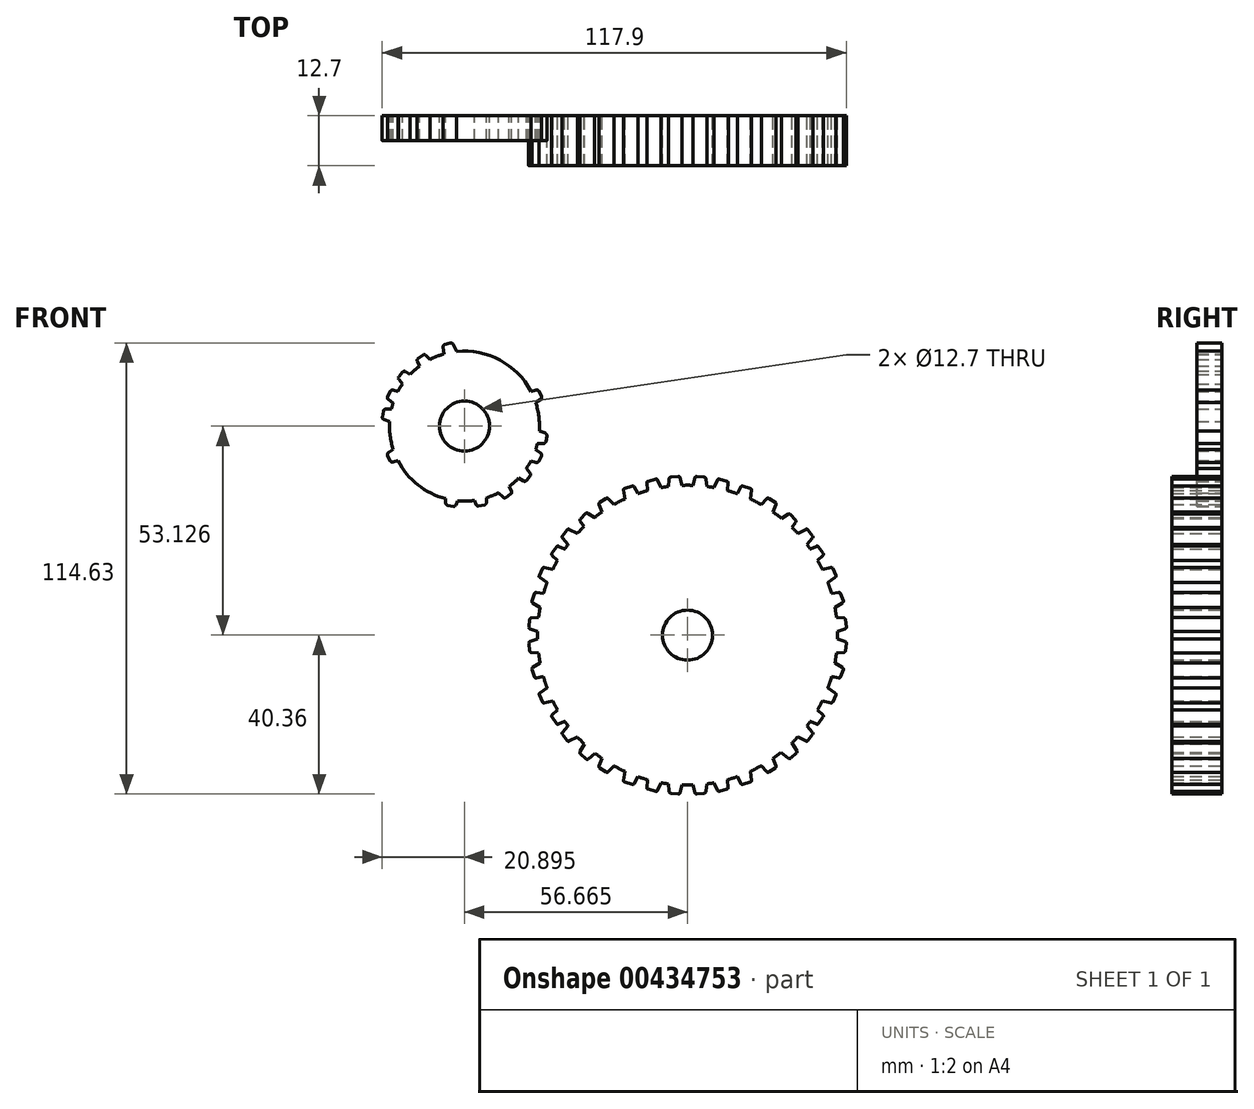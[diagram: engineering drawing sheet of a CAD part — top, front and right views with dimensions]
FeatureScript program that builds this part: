
annotation { "Feature Type Name" : "Feature", "Feature Type Description" : "" }
export const myFeature = defineFeature(function(context is Context, id is Id, definition is map)
    precondition{}
    {
        {
            var Q0;
            Q0=qCreatedBy(makeId("Front.planeOp"),FACE);
            var sketch = newSketch(context, id + "F0", { "sketchPlane" : qUnion([Q0])});
            skCircle(sketch, "E0", {"center": v(0, 0) * mm, "radius": 38.1 * mm});
            skCircle(sketch, "E1", {"center": v(0, 0) * mm, "radius": 6.35 * mm});
            skSolve(sketch);
        }
        {
            var Q0;
            Q0=makeQuery(id+"F0.imprint","IMPRINT",FACE,{"disambiguationData":[TD([[makeQuery(id+"F0.imprint","IMPRINT",EDGE,{"derivedFrom":sQuery(id+"F0.wireOp",EDGE,"E0")}),1.0]])]});
            extrude(context, id + "F1", {"entities" : qUnion([Q0]), "depth" : 12.7 * mm});
        }
        {
            var Q0;
            Q0=qCreatedBy(makeId("Front.planeOp"),FACE);
            var sketch = newSketch(context, id + "F2", { "sketchPlane" : qUnion([Q0])});
            skCircle(sketch, "E2", {"center": v(-56.67, 53.13) * mm, "radius": 19.05 * mm});
            skCircle(sketch, "E3", {"center": v(-56.67, 53.13) * mm, "radius": 6.35 * mm});
            skSolve(sketch);
        }
        {
            var Q0;
            Q0 = qSketchRegion(id + "F2", true);
            extrude(context, id + "F3", {"entities" : qUnion([Q0]), "depth" : 6.35 * mm});
        }
        {
            var Q0;
            Q0=qCreatedBy(makeId("Front.planeOp"),FACE);
            var sketch = newSketch(context, id + "F4", { "sketchPlane" : qUnion([Q0])});
            skLineSegment(sketch, "E4", {"start": v(-9.65, 35.42) * mm, "end": v(-6.58, 36.24) * mm});
            skLineSegment(sketch, "E5", {"start": v(-10.34, 38.75) * mm, "end": v(-10.2, 37.16) * mm});
            skLineSegment(sketch, "E6", {"start": v(-10.09, 39.1) * mm, "end": v(-8.05, 39.65) * mm});
            skLineSegment(sketch, "E7", {"start": v(-7.65, 39.47) * mm, "end": v(-6.37, 36.7) * mm});
            skLineSegment(sketch, "E8", {"start": v(-15.4, 33.61) * mm, "end": v(-12.37, 34.6) * mm});
            skLineSegment(sketch, "E9", {"start": v(-16.25, 36.9) * mm, "end": v(-15.83, 33.88) * mm});
            skLineSegment(sketch, "E10", {"start": v(-16.02, 37.27) * mm, "end": v(-14.01, 37.92) * mm});
            skLineSegment(sketch, "E11", {"start": v(-13.6, 37.76) * mm, "end": v(-12.18, 35.07) * mm});
            skLineSegment(sketch, "E12", {"start": v(-20.77, 30.34) * mm, "end": v(-18.25, 31.93) * mm});
            skLineSegment(sketch, "E13", {"start": v(-22.47, 33.21) * mm, "end": v(-21.38, 30.54) * mm});
            skLineSegment(sketch, "E14", {"start": v(-22.3, 33.72) * mm, "end": v(-20.7, 34.74) * mm});
            skLineSegment(sketch, "E15", {"start": v(-20.05, 34.65) * mm, "end": v(-18.16, 32.56) * mm});
            skLineSegment(sketch, "E16", {"start": v(-29.17, 22.58) * mm, "end": v(-27.36, 24.94) * mm});
            skLineSegment(sketch, "E17", {"start": v(-31.76, 24.68) * mm, "end": v(-29.82, 22.55) * mm});
            skLineSegment(sketch, "E18", {"start": v(-31.78, 25.22) * mm, "end": v(-30.58, 26.78) * mm});
            skLineSegment(sketch, "E19", {"start": v(-30.05, 26.9) * mm, "end": v(-27.5, 25.56) * mm});
            skLineSegment(sketch, "E20", {"start": v(-31.71, 18.3) * mm, "end": v(-30, 20.75) * mm});
            skLineSegment(sketch, "E21", {"start": v(-34.39, 20.3) * mm, "end": v(-32.35, 18.25) * mm});
            skLineSegment(sketch, "E22", {"start": v(-34.44, 20.83) * mm, "end": v(-33.3, 22.45) * mm});
            skLineSegment(sketch, "E23", {"start": v(-32.78, 22.59) * mm, "end": v(-30.17, 21.37) * mm});
            skLineSegment(sketch, "E24", {"start": v(-36.26, 7) * mm, "end": v(-35.25, 9.8) * mm});
            skLineSegment(sketch, "E25", {"start": v(-39.36, 8.22) * mm, "end": v(-36.87, 6.78) * mm});
            skLineSegment(sketch, "E26", {"start": v(-39.55, 8.73) * mm, "end": v(-38.87, 10.59) * mm});
            skLineSegment(sketch, "E27", {"start": v(-38.4, 10.86) * mm, "end": v(-35.57, 10.35) * mm});
            skLineSegment(sketch, "E28", {"start": v(-36.75, 1.08) * mm, "end": v(-36.37, 4.04) * mm});
            skLineSegment(sketch, "E29", {"start": v(-40.04, 1.59) * mm, "end": v(-37.29, 0.73) * mm});
            skLineSegment(sketch, "E30", {"start": v(-40.33, 2.04) * mm, "end": v(-40.08, 4) * mm});
            skLineSegment(sketch, "E31", {"start": v(-39.69, 4.37) * mm, "end": v(-36.81, 4.5) * mm});
            skLineSegment(sketch, "E32", {"start": v(-34.45, 13.26) * mm, "end": v(-33.3, 16) * mm});
            skLineSegment(sketch, "E33", {"start": v(-37.5, 14.6) * mm, "end": v(-35.06, 13.06) * mm});
            skLineSegment(sketch, "E34", {"start": v(-37.65, 15.12) * mm, "end": v(-36.9, 16.95) * mm});
            skLineSegment(sketch, "E35", {"start": v(-36.42, 17.2) * mm, "end": v(-33.6, 16.58) * mm});
            skLineSegment(sketch, "E36", {"start": v(-4.52, 36.48) * mm, "end": v(-1.55, 36.74) * mm});
            skLineSegment(sketch, "E37", {"start": v(-4.74, 39.57) * mm, "end": v(-4.97, 36.94) * mm});
            skLineSegment(sketch, "E38", {"start": v(-4.1, 40.2) * mm, "end": v(-2.37, 40.36) * mm});
            skLineSegment(sketch, "E39", {"start": v(-1.93, 40.05) * mm, "end": v(-1.18, 37.27) * mm});
            skPoint(sketch, "E40.visualSharp", {"position": v(-16.3, 37.18) * mm});
            skArc(sketch, "E40.filletArc", {"start": v(-16.02, 37.27) * mm, "mid": v(-16.2, 37.13) * mm, "end": v(-16.25, 36.9) * mm});
            skPoint(sketch, "E41.visualSharp", {"position": v(-13.74, 38.01) * mm});
            skArc(sketch, "E41.filletArc", {"start": v(-13.6, 37.76) * mm, "mid": v(-13.78, 37.92) * mm, "end": v(-14.01, 37.92) * mm});
            skPoint(sketch, "E42.visualSharp", {"position": v(-12, 34.71) * mm});
            skArc(sketch, "E42.filletArc", {"start": v(-12.37, 34.6) * mm, "mid": v(-12.16, 34.78) * mm, "end": v(-12.18, 35.07) * mm});
            skPoint(sketch, "E43.visualSharp", {"position": v(-15.77, 33.49) * mm});
            skArc(sketch, "E43.filletArc", {"start": v(-15.83, 33.88) * mm, "mid": v(-15.67, 33.65) * mm, "end": v(-15.4, 33.61) * mm});
            skPoint(sketch, "E44.visualSharp", {"position": v(-10.04, 35.31) * mm});
            skArc(sketch, "E44.filletArc", {"start": v(-10.07, 35.71) * mm, "mid": v(-9.93, 35.47) * mm, "end": v(-9.65, 35.42) * mm});
            skPoint(sketch, "E45.visualSharp", {"position": v(-10.36, 39.03) * mm});
            skArc(sketch, "E45.filletArc", {"start": v(-10.09, 39.1) * mm, "mid": v(-10.28, 38.97) * mm, "end": v(-10.34, 38.75) * mm});
            skPoint(sketch, "E46.visualSharp", {"position": v(-7.77, 39.72) * mm});
            skArc(sketch, "E46.filletArc", {"start": v(-7.65, 39.47) * mm, "mid": v(-7.82, 39.63) * mm, "end": v(-8.05, 39.65) * mm});
            skPoint(sketch, "E47.visualSharp", {"position": v(-6.2, 36.34) * mm});
            skArc(sketch, "E47.filletArc", {"start": v(-6.58, 36.24) * mm, "mid": v(-6.37, 36.42) * mm, "end": v(-6.37, 36.7) * mm});
            skPoint(sketch, "E48.visualSharp", {"position": v(-4.7, 40.16) * mm});
            skArc(sketch, "E48.filletArc", {"start": v(-4.1, 40.2) * mm, "mid": v(-4.54, 40) * mm, "end": v(-4.74, 39.57) * mm});
            skPoint(sketch, "E49.visualSharp", {"position": v(-20.33, 34.96) * mm});
            skArc(sketch, "E49.filletArc", {"start": v(-20.05, 34.65) * mm, "mid": v(-20.36, 34.8) * mm, "end": v(-20.7, 34.74) * mm});
            skPoint(sketch, "E50.visualSharp", {"position": v(-22.6, 33.54) * mm});
            skArc(sketch, "E50.filletArc", {"start": v(-22.3, 33.72) * mm, "mid": v(-22.48, 33.5) * mm, "end": v(-22.47, 33.21) * mm});
            skPoint(sketch, "E51.visualSharp", {"position": v(-21.17, 30.31) * mm});
            skArc(sketch, "E51.filletArc", {"start": v(-21.38, 30.54) * mm, "mid": v(-21.12, 30.3) * mm, "end": v(-20.77, 30.34) * mm});
            skPoint(sketch, "E52.visualSharp", {"position": v(-17.83, 32.2) * mm});
            skArc(sketch, "E52.filletArc", {"start": v(-18.25, 31.93) * mm, "mid": v(-18.06, 32.23) * mm, "end": v(-18.16, 32.56) * mm});
            skPoint(sketch, "E53.visualSharp", {"position": v(-2.02, 40.4) * mm});
            skArc(sketch, "E53.filletArc", {"start": v(-1.93, 40.05) * mm, "mid": v(-2.1, 40.29) * mm, "end": v(-2.37, 40.36) * mm});
            skArc(sketch, "E54.filletArc", {"start": v(-4.97, 36.94) * mm, "mid": v(-4.85, 36.6) * mm, "end": v(-4.52, 36.48) * mm});
            skPoint(sketch, "E55.visualSharp", {"position": v(-1.05, 36.79) * mm});
            skArc(sketch, "E55.filletArc", {"start": v(-1.55, 36.74) * mm, "mid": v(-1.25, 36.92) * mm, "end": v(-1.18, 37.27) * mm});
            skLineSegment(sketch, "E56", {"start": v(-10.2, 37.16) * mm, "end": v(-10.07, 35.71) * mm});
            skLineSegment(sketch, "E57", {"start": v(-10.07, 35.71) * mm, "end": v(-10.11, 36.17) * mm});
            skLineSegment(sketch, "E58", {"start": v(-10.11, 36.17) * mm, "end": v(-10.07, 35.71) * mm});
            skPoint(sketch, "E59.visualSharp", {"position": v(-25.7, 26.26) * mm});
            skPoint(sketch, "E60.visualSharp", {"position": v(-32, 24.94) * mm});
            skArc(sketch, "E60.filletArc", {"start": v(-31.78, 25.22) * mm, "mid": v(-31.87, 24.94) * mm, "end": v(-31.76, 24.68) * mm});
            skPoint(sketch, "E61.visualSharp", {"position": v(-30.36, 27.06) * mm});
            skArc(sketch, "E61.filletArc", {"start": v(-30.05, 26.9) * mm, "mid": v(-30.34, 26.94) * mm, "end": v(-30.58, 26.78) * mm});
            skPoint(sketch, "E62.visualSharp", {"position": v(-29.48, 22.18) * mm});
            skArc(sketch, "E62.filletArc", {"start": v(-29.82, 22.55) * mm, "mid": v(-29.49, 22.41) * mm, "end": v(-29.17, 22.58) * mm});
            skPoint(sketch, "E63.visualSharp", {"position": v(-27.05, 25.33) * mm});
            skArc(sketch, "E63.filletArc", {"start": v(-27.36, 24.94) * mm, "mid": v(-27.28, 25.28) * mm, "end": v(-27.5, 25.56) * mm});
            skPoint(sketch, "E64.visualSharp", {"position": v(-33.1, 22.73) * mm});
            skArc(sketch, "E64.filletArc", {"start": v(-32.78, 22.59) * mm, "mid": v(-33.07, 22.61) * mm, "end": v(-33.3, 22.45) * mm});
            skPoint(sketch, "E65.visualSharp", {"position": v(-34.64, 20.54) * mm});
            skArc(sketch, "E65.filletArc", {"start": v(-34.44, 20.83) * mm, "mid": v(-34.5, 20.55) * mm, "end": v(-34.39, 20.3) * mm});
            skPoint(sketch, "E66.visualSharp", {"position": v(-32, 17.9) * mm});
            skArc(sketch, "E66.filletArc", {"start": v(-32.35, 18.25) * mm, "mid": v(-32.02, 18.13) * mm, "end": v(-31.71, 18.3) * mm});
            skPoint(sketch, "E67.visualSharp", {"position": v(-29.72, 21.16) * mm});
            skArc(sketch, "E67.filletArc", {"start": v(-30, 20.75) * mm, "mid": v(-29.94, 21.1) * mm, "end": v(-30.17, 21.37) * mm});
            skPoint(sketch, "E68.visualSharp", {"position": v(-36.76, 17.27) * mm});
            skArc(sketch, "E68.filletArc", {"start": v(-36.42, 17.2) * mm, "mid": v(-36.7, 17.16) * mm, "end": v(-36.9, 16.95) * mm});
            skPoint(sketch, "E69.visualSharp", {"position": v(-37.79, 14.8) * mm});
            skArc(sketch, "E69.filletArc", {"start": v(-37.65, 15.12) * mm, "mid": v(-37.66, 14.84) * mm, "end": v(-37.5, 14.6) * mm});
            skPoint(sketch, "E70.visualSharp", {"position": v(-34.64, 12.8) * mm});
            skArc(sketch, "E70.filletArc", {"start": v(-35.06, 13.06) * mm, "mid": v(-34.7, 13.02) * mm, "end": v(-34.45, 13.26) * mm});
            skPoint(sketch, "E71.visualSharp", {"position": v(-33.12, 16.47) * mm});
            skArc(sketch, "E71.filletArc", {"start": v(-33.3, 16) * mm, "mid": v(-33.32, 16.36) * mm, "end": v(-33.6, 16.58) * mm});
            skPoint(sketch, "E72.visualSharp", {"position": v(-38.75, 10.92) * mm});
            skArc(sketch, "E72.filletArc", {"start": v(-38.4, 10.86) * mm, "mid": v(-38.69, 10.8) * mm, "end": v(-38.87, 10.59) * mm});
            skPoint(sketch, "E73.visualSharp", {"position": v(-39.67, 8.4) * mm});
            skArc(sketch, "E73.filletArc", {"start": v(-39.55, 8.73) * mm, "mid": v(-39.55, 8.44) * mm, "end": v(-39.36, 8.22) * mm});
            skPoint(sketch, "E74.visualSharp", {"position": v(-36.43, 6.53) * mm});
            skArc(sketch, "E74.filletArc", {"start": v(-36.87, 6.78) * mm, "mid": v(-36.51, 6.75) * mm, "end": v(-36.26, 7) * mm});
            skPoint(sketch, "E75.visualSharp", {"position": v(-35.08, 10.27) * mm});
            skArc(sketch, "E75.filletArc", {"start": v(-35.25, 9.8) * mm, "mid": v(-35.28, 10.15) * mm, "end": v(-35.57, 10.35) * mm});
            skPoint(sketch, "E76.visualSharp", {"position": v(-40.04, 4.35) * mm});
            skArc(sketch, "E76.filletArc", {"start": v(-39.69, 4.37) * mm, "mid": v(-39.95, 4.26) * mm, "end": v(-40.08, 4) * mm});
            skPoint(sketch, "E77.visualSharp", {"position": v(-40.38, 1.7) * mm});
            skArc(sketch, "E77.filletArc", {"start": v(-40.33, 2.04) * mm, "mid": v(-40.27, 1.76) * mm, "end": v(-40.04, 1.59) * mm});
            skPoint(sketch, "E78.visualSharp", {"position": v(-36.81, 0.59) * mm});
            skArc(sketch, "E78.filletArc", {"start": v(-37.29, 0.73) * mm, "mid": v(-36.94, 0.78) * mm, "end": v(-36.75, 1.08) * mm});
            skPoint(sketch, "E79.visualSharp", {"position": v(-36.31, 4.53) * mm});
            skArc(sketch, "E79.filletArc", {"start": v(-36.37, 4.04) * mm, "mid": v(-36.48, 4.37) * mm, "end": v(-36.81, 4.5) * mm});
            skLineSegment(sketch, "E80", {"start": v(0, 38.16) * mm, "end": v(0, 0) * mm});
            skLineSegment(sketch, "E81.MirrorCS", {"start": v(10.07, 35.71) * mm, "end": v(10.11, 36.17) * mm});
            skArc(sketch, "E82.MirrorCS", {"start": v(10.07, 35.71) * mm, "mid": v(9.93, 35.47) * mm, "end": v(9.65, 35.42) * mm});
            skLineSegment(sketch, "E83.MirrorCS", {"start": v(10.11, 36.17) * mm, "end": v(10.07, 35.71) * mm});
            skArc(sketch, "E84.MirrorCS", {"start": v(1.93, 40.05) * mm, "mid": v(2.1, 40.29) * mm, "end": v(2.37, 40.36) * mm});
            skArc(sketch, "E85.MirrorCS", {"start": v(7.65, 39.47) * mm, "mid": v(7.82, 39.63) * mm, "end": v(8.05, 39.65) * mm});
            skArc(sketch, "E86.MirrorCS", {"start": v(39.55, 8.73) * mm, "mid": v(39.55, 8.44) * mm, "end": v(39.36, 8.22) * mm});
            skArc(sketch, "E87.MirrorCS", {"start": v(32.35, 18.25) * mm, "mid": v(32.02, 18.13) * mm, "end": v(31.71, 18.3) * mm});
            skArc(sketch, "E88.MirrorCS", {"start": v(6.58, 36.24) * mm, "mid": v(6.37, 36.42) * mm, "end": v(6.37, 36.7) * mm});
            skArc(sketch, "E89.MirrorCS", {"start": v(39.69, 4.37) * mm, "mid": v(39.95, 4.26) * mm, "end": v(40.08, 4) * mm});
            skLineSegment(sketch, "E90.MirrorCS", {"start": v(34.44, 20.83) * mm, "end": v(33.3, 22.45) * mm});
            skArc(sketch, "E91.MirrorCS", {"start": v(31.78, 25.22) * mm, "mid": v(31.87, 24.94) * mm, "end": v(31.76, 24.68) * mm});
            skArc(sketch, "E92.MirrorCS", {"start": v(30, 20.75) * mm, "mid": v(29.94, 21.1) * mm, "end": v(30.17, 21.37) * mm});
            skArc(sketch, "E93.MirrorCS", {"start": v(40.33, 2.04) * mm, "mid": v(40.27, 1.76) * mm, "end": v(40.04, 1.59) * mm});
            skArc(sketch, "E94.MirrorCS", {"start": v(30.05, 26.9) * mm, "mid": v(30.34, 26.94) * mm, "end": v(30.58, 26.78) * mm});
            skArc(sketch, "E95.MirrorCS", {"start": v(35.25, 9.8) * mm, "mid": v(35.28, 10.15) * mm, "end": v(35.57, 10.35) * mm});
            skArc(sketch, "E96.MirrorCS", {"start": v(34.44, 20.83) * mm, "mid": v(34.5, 20.55) * mm, "end": v(34.39, 20.3) * mm});
            skArc(sketch, "E97.MirrorCS", {"start": v(10.09, 39.1) * mm, "mid": v(10.28, 38.97) * mm, "end": v(10.34, 38.75) * mm});
            skArc(sketch, "E98.MirrorCS", {"start": v(27.36, 24.94) * mm, "mid": v(27.28, 25.28) * mm, "end": v(27.5, 25.56) * mm});
            skArc(sketch, "E99.MirrorCS", {"start": v(36.37, 4.04) * mm, "mid": v(36.48, 4.37) * mm, "end": v(36.81, 4.5) * mm});
            skArc(sketch, "E100.MirrorCS", {"start": v(38.4, 10.86) * mm, "mid": v(38.69, 10.8) * mm, "end": v(38.87, 10.59) * mm});
            skLineSegment(sketch, "E101.MirrorCS", {"start": v(31.78, 25.22) * mm, "end": v(30.58, 26.78) * mm});
            skArc(sketch, "E102.MirrorCS", {"start": v(22.3, 33.72) * mm, "mid": v(22.48, 33.5) * mm, "end": v(22.47, 33.21) * mm});
            skArc(sketch, "E103.MirrorCS", {"start": v(21.38, 30.54) * mm, "mid": v(21.12, 30.3) * mm, "end": v(20.77, 30.34) * mm});
            skArc(sketch, "E104.MirrorCS", {"start": v(13.6, 37.76) * mm, "mid": v(13.78, 37.92) * mm, "end": v(14.01, 37.92) * mm});
            skArc(sketch, "E105.MirrorCS", {"start": v(36.42, 17.2) * mm, "mid": v(36.7, 17.16) * mm, "end": v(36.9, 16.95) * mm});
            skArc(sketch, "E106.MirrorCS", {"start": v(20.05, 34.65) * mm, "mid": v(20.36, 34.8) * mm, "end": v(20.7, 34.74) * mm});
            skArc(sketch, "E107.MirrorCS", {"start": v(32.78, 22.59) * mm, "mid": v(33.07, 22.61) * mm, "end": v(33.3, 22.45) * mm});
            skArc(sketch, "E108.MirrorCS", {"start": v(12.37, 34.6) * mm, "mid": v(12.16, 34.78) * mm, "end": v(12.18, 35.07) * mm});
            skArc(sketch, "E109.MirrorCS", {"start": v(15.83, 33.88) * mm, "mid": v(15.67, 33.65) * mm, "end": v(15.4, 33.61) * mm});
            skArc(sketch, "E110.MirrorCS", {"start": v(16.02, 37.27) * mm, "mid": v(16.2, 37.13) * mm, "end": v(16.25, 36.9) * mm});
            skArc(sketch, "E111.MirrorCS", {"start": v(37.65, 15.12) * mm, "mid": v(37.66, 14.84) * mm, "end": v(37.5, 14.6) * mm});
            skArc(sketch, "E112.MirrorCS", {"start": v(4.97, 36.94) * mm, "mid": v(4.85, 36.6) * mm, "end": v(4.52, 36.48) * mm});
            skArc(sketch, "E113.MirrorCS", {"start": v(4.1, 40.2) * mm, "mid": v(4.54, 40) * mm, "end": v(4.74, 39.57) * mm});
            skArc(sketch, "E114.MirrorCS", {"start": v(36.87, 6.78) * mm, "mid": v(36.51, 6.75) * mm, "end": v(36.26, 7) * mm});
            skArc(sketch, "E115.MirrorCS", {"start": v(18.25, 31.93) * mm, "mid": v(18.06, 32.23) * mm, "end": v(18.16, 32.56) * mm});
            skArc(sketch, "E116.MirrorCS", {"start": v(37.29, 0.73) * mm, "mid": v(36.94, 0.78) * mm, "end": v(36.75, 1.08) * mm});
            skArc(sketch, "E117.MirrorCS", {"start": v(35.06, 13.06) * mm, "mid": v(34.7, 13.02) * mm, "end": v(34.45, 13.26) * mm});
            skLineSegment(sketch, "E118.MirrorCS", {"start": v(10.34, 38.75) * mm, "end": v(10.2, 37.16) * mm});
            skArc(sketch, "E119.MirrorCS", {"start": v(33.3, 16) * mm, "mid": v(33.32, 16.36) * mm, "end": v(33.6, 16.58) * mm});
            skLineSegment(sketch, "E120.MirrorCS", {"start": v(10.2, 37.16) * mm, "end": v(10.07, 35.71) * mm});
            skArc(sketch, "E121.MirrorCS", {"start": v(1.55, 36.74) * mm, "mid": v(1.25, 36.92) * mm, "end": v(1.18, 37.27) * mm});
            skArc(sketch, "E122.MirrorCS", {"start": v(29.82, 22.55) * mm, "mid": v(29.49, 22.41) * mm, "end": v(29.17, 22.58) * mm});
            skLineSegment(sketch, "E123.MirrorCS", {"start": v(34.39, 20.3) * mm, "end": v(32.35, 18.25) * mm});
            skLineSegment(sketch, "E124.MirrorCS", {"start": v(4.74, 39.57) * mm, "end": v(4.97, 36.94) * mm});
            skLineSegment(sketch, "E125.MirrorCS", {"start": v(40.33, 2.04) * mm, "end": v(40.08, 4) * mm});
            skLineSegment(sketch, "E126.MirrorCS", {"start": v(36.75, 1.08) * mm, "end": v(36.37, 4.04) * mm});
            skPoint(sketch, "E127.MirrorP", {"position": v(36.31, 4.53) * mm});
            skPoint(sketch, "E128.MirrorP", {"position": v(15.77, 33.49) * mm});
            skPoint(sketch, "E129.MirrorP", {"position": v(1.05, 36.79) * mm});
            skPoint(sketch, "E130.MirrorP", {"position": v(21.17, 30.31) * mm});
            skPoint(sketch, "E131.MirrorP", {"position": v(36.76, 17.27) * mm});
            skPoint(sketch, "E132.MirrorP", {"position": v(32, 24.94) * mm});
            skPoint(sketch, "E133.MirrorP", {"position": v(27.05, 25.33) * mm});
            skPoint(sketch, "E134.MirrorP", {"position": v(33.12, 16.47) * mm});
            skPoint(sketch, "E135.MirrorP", {"position": v(6.2, 36.34) * mm});
            skPoint(sketch, "E136.MirrorP", {"position": v(40.04, 4.35) * mm});
            skLineSegment(sketch, "E137.MirrorCS", {"start": v(39.69, 4.37) * mm, "end": v(36.81, 4.5) * mm});
            skLineSegment(sketch, "E138.MirrorCS", {"start": v(4.1, 40.2) * mm, "end": v(2.37, 40.36) * mm});
            skLineSegment(sketch, "E139.MirrorCS", {"start": v(34.45, 13.26) * mm, "end": v(33.3, 16) * mm});
            skLineSegment(sketch, "E140.MirrorCS", {"start": v(29.17, 22.58) * mm, "end": v(27.36, 24.94) * mm});
            skPoint(sketch, "E141.MirrorP", {"position": v(32, 17.9) * mm});
            skPoint(sketch, "E142.MirrorP", {"position": v(36.43, 6.53) * mm});
            skPoint(sketch, "E143.MirrorP", {"position": v(38.75, 10.92) * mm});
            skPoint(sketch, "E144.MirrorP", {"position": v(33.1, 22.73) * mm});
            skLineSegment(sketch, "E145.MirrorCS", {"start": v(32.78, 22.59) * mm, "end": v(30.17, 21.37) * mm});
            skPoint(sketch, "E146.MirrorP", {"position": v(10.04, 35.31) * mm});
            skLineSegment(sketch, "E147.MirrorCS", {"start": v(4.52, 36.48) * mm, "end": v(1.55, 36.74) * mm});
            skLineSegment(sketch, "E148.MirrorCS", {"start": v(22.3, 33.72) * mm, "end": v(20.7, 34.74) * mm});
            skLineSegment(sketch, "E149.MirrorCS", {"start": v(22.47, 33.21) * mm, "end": v(21.38, 30.54) * mm});
            skLineSegment(sketch, "E150.MirrorCS", {"start": v(20.05, 34.65) * mm, "end": v(18.16, 32.56) * mm});
            skLineSegment(sketch, "E151.MirrorCS", {"start": v(20.77, 30.34) * mm, "end": v(18.25, 31.93) * mm});
            skPoint(sketch, "E152.MirrorP", {"position": v(22.6, 33.54) * mm});
            skLineSegment(sketch, "E153.MirrorCS", {"start": v(1.93, 40.05) * mm, "end": v(1.18, 37.27) * mm});
            skPoint(sketch, "E154.MirrorP", {"position": v(29.72, 21.16) * mm});
            skPoint(sketch, "E155.MirrorP", {"position": v(35.08, 10.27) * mm});
            skPoint(sketch, "E156.MirrorP", {"position": v(34.64, 12.8) * mm});
            skLineSegment(sketch, "E157.MirrorCS", {"start": v(9.65, 35.42) * mm, "end": v(6.58, 36.24) * mm});
            skPoint(sketch, "E158.MirrorP", {"position": v(20.33, 34.96) * mm});
            skLineSegment(sketch, "E159.MirrorCS", {"start": v(36.42, 17.2) * mm, "end": v(33.6, 16.58) * mm});
            skLineSegment(sketch, "E160.MirrorCS", {"start": v(40.04, 1.59) * mm, "end": v(37.29, 0.73) * mm});
            skLineSegment(sketch, "E161.MirrorCS", {"start": v(37.65, 15.12) * mm, "end": v(36.9, 16.95) * mm});
            skLineSegment(sketch, "E162.MirrorCS", {"start": v(13.6, 37.76) * mm, "end": v(12.18, 35.07) * mm});
            skLineSegment(sketch, "E163.MirrorCS", {"start": v(15.4, 33.61) * mm, "end": v(12.37, 34.6) * mm});
            skPoint(sketch, "E164.MirrorP", {"position": v(12, 34.71) * mm});
            skPoint(sketch, "E165.MirrorP", {"position": v(2.02, 40.4) * mm});
            skLineSegment(sketch, "E166.MirrorCS", {"start": v(38.4, 10.86) * mm, "end": v(35.57, 10.35) * mm});
            skLineSegment(sketch, "E167.MirrorCS", {"start": v(7.65, 39.47) * mm, "end": v(6.37, 36.7) * mm});
            skPoint(sketch, "E168.MirrorP", {"position": v(10.36, 39.03) * mm});
            skLineSegment(sketch, "E169.MirrorCS", {"start": v(10.09, 39.1) * mm, "end": v(8.05, 39.65) * mm});
            skLineSegment(sketch, "E170.MirrorCS", {"start": v(39.36, 8.22) * mm, "end": v(36.87, 6.78) * mm});
            skPoint(sketch, "E171.MirrorP", {"position": v(39.67, 8.4) * mm});
            skPoint(sketch, "E172.MirrorP", {"position": v(34.64, 20.54) * mm});
            skPoint(sketch, "E173.MirrorP", {"position": v(7.77, 39.72) * mm});
            skLineSegment(sketch, "E174.MirrorCS", {"start": v(37.5, 14.6) * mm, "end": v(35.06, 13.06) * mm});
            skPoint(sketch, "E175.MirrorP", {"position": v(40.38, 1.7) * mm});
            skLineSegment(sketch, "E176.MirrorCS", {"start": v(31.76, 24.68) * mm, "end": v(29.82, 22.55) * mm});
            skPoint(sketch, "E177.MirrorP", {"position": v(30.36, 27.06) * mm});
            skLineSegment(sketch, "E178.MirrorCS", {"start": v(39.55, 8.73) * mm, "end": v(38.87, 10.59) * mm});
            skLineSegment(sketch, "E179.MirrorCS", {"start": v(30.05, 26.9) * mm, "end": v(27.5, 25.56) * mm});
            skPoint(sketch, "E180.MirrorP", {"position": v(29.48, 22.18) * mm});
            skLineSegment(sketch, "E181.MirrorCS", {"start": v(31.71, 18.3) * mm, "end": v(30, 20.75) * mm});
            skPoint(sketch, "E182.MirrorP", {"position": v(37.79, 14.8) * mm});
            skPoint(sketch, "E183.MirrorP", {"position": v(36.81, 0.59) * mm});
            skLineSegment(sketch, "E184.MirrorCS", {"start": v(16.25, 36.9) * mm, "end": v(15.83, 33.88) * mm});
            skPoint(sketch, "E185.MirrorP", {"position": v(13.74, 38.01) * mm});
            skPoint(sketch, "E186.MirrorP", {"position": v(17.83, 32.2) * mm});
            skLineSegment(sketch, "E187.MirrorCS", {"start": v(36.26, 7) * mm, "end": v(35.25, 9.8) * mm});
            skPoint(sketch, "E188.MirrorP", {"position": v(16.3, 37.18) * mm});
            skLineSegment(sketch, "E189.MirrorCS", {"start": v(16.02, 37.27) * mm, "end": v(14.01, 37.92) * mm});
            skPoint(sketch, "E190.MirrorP", {"position": v(4.7, 40.16) * mm});
            skLineSegment(sketch, "E191", {"start": v(-38.12, 0) * mm, "end": v(38.16, 0) * mm});
            skPoint(sketch, "E191.startSnap0", {"position": v(-38.12, 7.5) * mm});
            skLineSegment(sketch, "E192.MirrorCS", {"start": v(10.11, -36.17) * mm, "end": v(10.07, -35.71) * mm});
            skLineSegment(sketch, "E193.MirrorCS", {"start": v(-10.07, -35.71) * mm, "end": v(-10.11, -36.17) * mm});
            skLineSegment(sketch, "E194.MirrorCS", {"start": v(10.07, -35.71) * mm, "end": v(10.11, -36.17) * mm});
            skArc(sketch, "E195.MirrorCS", {"start": v(10.07, -35.71) * mm, "mid": v(9.93, -35.47) * mm, "end": v(9.65, -35.42) * mm});
            skLineSegment(sketch, "E196.MirrorCS", {"start": v(-10.11, -36.17) * mm, "end": v(-10.07, -35.71) * mm});
            skArc(sketch, "E197.MirrorCS", {"start": v(-10.07, -35.71) * mm, "mid": v(-9.93, -35.47) * mm, "end": v(-9.65, -35.42) * mm});
            skArc(sketch, "E198.MirrorCS", {"start": v(16.02, -37.27) * mm, "mid": v(16.2, -37.13) * mm, "end": v(16.25, -36.9) * mm});
            skArc(sketch, "E199.MirrorCS", {"start": v(-30, -20.75) * mm, "mid": v(-29.94, -21.1) * mm, "end": v(-30.17, -21.37) * mm});
            skArc(sketch, "E200.MirrorCS", {"start": v(-36.42, -17.2) * mm, "mid": v(-36.7, -17.16) * mm, "end": v(-36.9, -16.95) * mm});
            skArc(sketch, "E201.MirrorCS", {"start": v(-1.55, -36.74) * mm, "mid": v(-1.25, -36.92) * mm, "end": v(-1.18, -37.27) * mm});
            skArc(sketch, "E202.MirrorCS", {"start": v(10.09, -39.1) * mm, "mid": v(10.28, -38.97) * mm, "end": v(10.34, -38.75) * mm});
            skArc(sketch, "E203.MirrorCS", {"start": v(37.65, -15.12) * mm, "mid": v(37.66, -14.84) * mm, "end": v(37.5, -14.6) * mm});
            skArc(sketch, "E204.MirrorCS", {"start": v(1.93, -40.05) * mm, "mid": v(2.1, -40.29) * mm, "end": v(2.37, -40.36) * mm});
            skArc(sketch, "E205.MirrorCS", {"start": v(-37.65, -15.12) * mm, "mid": v(-37.66, -14.84) * mm, "end": v(-37.5, -14.6) * mm});
            skArc(sketch, "E206.MirrorCS", {"start": v(-16.02, -37.27) * mm, "mid": v(-16.2, -37.13) * mm, "end": v(-16.25, -36.9) * mm});
            skArc(sketch, "E207.MirrorCS", {"start": v(7.65, -39.47) * mm, "mid": v(7.82, -39.63) * mm, "end": v(8.05, -39.65) * mm});
            skArc(sketch, "E208.MirrorCS", {"start": v(-35.06, -13.06) * mm, "mid": v(-34.7, -13.02) * mm, "end": v(-34.45, -13.26) * mm});
            skArc(sketch, "E209.MirrorCS", {"start": v(-13.6, -37.76) * mm, "mid": v(-13.78, -37.92) * mm, "end": v(-14.01, -37.92) * mm});
            skArc(sketch, "E210.MirrorCS", {"start": v(39.55, -8.73) * mm, "mid": v(39.55, -8.44) * mm, "end": v(39.36, -8.22) * mm});
            skArc(sketch, "E211.MirrorCS", {"start": v(-33.3, -16) * mm, "mid": v(-33.32, -16.36) * mm, "end": v(-33.6, -16.58) * mm});
            skArc(sketch, "E212.MirrorCS", {"start": v(-12.37, -34.6) * mm, "mid": v(-12.16, -34.78) * mm, "end": v(-12.18, -35.07) * mm});
            skArc(sketch, "E213.MirrorCS", {"start": v(27.36, -24.94) * mm, "mid": v(27.28, -25.28) * mm, "end": v(27.5, -25.56) * mm});
            skArc(sketch, "E214.MirrorCS", {"start": v(-38.4, -10.86) * mm, "mid": v(-38.69, -10.8) * mm, "end": v(-38.87, -10.59) * mm});
            skArc(sketch, "E215.MirrorCS", {"start": v(-15.83, -33.88) * mm, "mid": v(-15.67, -33.65) * mm, "end": v(-15.4, -33.61) * mm});
            skArc(sketch, "E216.MirrorCS", {"start": v(36.87, -6.78) * mm, "mid": v(36.51, -6.75) * mm, "end": v(36.26, -7) * mm});
            skArc(sketch, "E217.MirrorCS", {"start": v(-10.09, -39.1) * mm, "mid": v(-10.28, -38.97) * mm, "end": v(-10.34, -38.75) * mm});
            skArc(sketch, "E218.MirrorCS", {"start": v(6.58, -36.24) * mm, "mid": v(6.37, -36.42) * mm, "end": v(6.37, -36.7) * mm});
            skArc(sketch, "E219.MirrorCS", {"start": v(-36.87, -6.78) * mm, "mid": v(-36.51, -6.75) * mm, "end": v(-36.26, -7) * mm});
            skArc(sketch, "E220.MirrorCS", {"start": v(32.35, -18.25) * mm, "mid": v(32.02, -18.13) * mm, "end": v(31.71, -18.3) * mm});
            skArc(sketch, "E221.MirrorCS", {"start": v(-39.55, -8.73) * mm, "mid": v(-39.55, -8.44) * mm, "end": v(-39.36, -8.22) * mm});
            skArc(sketch, "E222.MirrorCS", {"start": v(18.25, -31.93) * mm, "mid": v(18.06, -32.23) * mm, "end": v(18.16, -32.56) * mm});
            skArc(sketch, "E223.MirrorCS", {"start": v(38.4, -10.86) * mm, "mid": v(38.69, -10.8) * mm, "end": v(38.87, -10.59) * mm});
            skArc(sketch, "E224.MirrorCS", {"start": v(-7.65, -39.47) * mm, "mid": v(-7.82, -39.63) * mm, "end": v(-8.05, -39.65) * mm});
            skArc(sketch, "E225.MirrorCS", {"start": v(22.3, -33.72) * mm, "mid": v(22.48, -33.5) * mm, "end": v(22.47, -33.21) * mm});
            skArc(sketch, "E226.MirrorCS", {"start": v(39.69, -4.37) * mm, "mid": v(39.95, -4.26) * mm, "end": v(40.08, -4) * mm});
            skArc(sketch, "E227.MirrorCS", {"start": v(34.44, -20.83) * mm, "mid": v(34.5, -20.55) * mm, "end": v(34.39, -20.3) * mm});
            skArc(sketch, "E228.MirrorCS", {"start": v(15.83, -33.88) * mm, "mid": v(15.67, -33.65) * mm, "end": v(15.4, -33.61) * mm});
            skArc(sketch, "E229.MirrorCS", {"start": v(1.55, -36.74) * mm, "mid": v(1.25, -36.92) * mm, "end": v(1.18, -37.27) * mm});
            skArc(sketch, "E230.MirrorCS", {"start": v(-22.3, -33.72) * mm, "mid": v(-22.48, -33.5) * mm, "end": v(-22.47, -33.21) * mm});
            skArc(sketch, "E231.MirrorCS", {"start": v(35.06, -13.06) * mm, "mid": v(34.7, -13.02) * mm, "end": v(34.45, -13.26) * mm});
            skArc(sketch, "E232.MirrorCS", {"start": v(-1.93, -40.05) * mm, "mid": v(-2.1, -40.29) * mm, "end": v(-2.37, -40.36) * mm});
            skArc(sketch, "E233.MirrorCS", {"start": v(20.05, -34.65) * mm, "mid": v(20.36, -34.8) * mm, "end": v(20.7, -34.74) * mm});
            skArc(sketch, "E234.MirrorCS", {"start": v(40.33, -2.04) * mm, "mid": v(40.27, -1.76) * mm, "end": v(40.04, -1.59) * mm});
            skArc(sketch, "E235.MirrorCS", {"start": v(-20.05, -34.65) * mm, "mid": v(-20.36, -34.8) * mm, "end": v(-20.7, -34.74) * mm});
            skArc(sketch, "E236.MirrorCS", {"start": v(30, -20.75) * mm, "mid": v(29.94, -21.1) * mm, "end": v(30.17, -21.37) * mm});
            skArc(sketch, "E237.MirrorCS", {"start": v(36.42, -17.2) * mm, "mid": v(36.7, -17.16) * mm, "end": v(36.9, -16.95) * mm});
            skLineSegment(sketch, "E238.MirrorCS", {"start": v(22.3, -33.72) * mm, "end": v(20.7, -34.74) * mm});
            skLineSegment(sketch, "E239.MirrorCS", {"start": v(-22.3, -33.72) * mm, "end": v(-20.7, -34.74) * mm});
            skArc(sketch, "E240.MirrorCS", {"start": v(33.3, -16) * mm, "mid": v(33.32, -16.36) * mm, "end": v(33.6, -16.58) * mm});
            skArc(sketch, "E241.MirrorCS", {"start": v(-30.05, -26.9) * mm, "mid": v(-30.34, -26.94) * mm, "end": v(-30.58, -26.78) * mm});
            skArc(sketch, "E242.MirrorCS", {"start": v(31.78, -25.22) * mm, "mid": v(31.87, -24.94) * mm, "end": v(31.76, -24.68) * mm});
            skArc(sketch, "E243.MirrorCS", {"start": v(-34.44, -20.83) * mm, "mid": v(-34.5, -20.55) * mm, "end": v(-34.39, -20.3) * mm});
            skArc(sketch, "E244.MirrorCS", {"start": v(-40.33, -2.04) * mm, "mid": v(-40.27, -1.76) * mm, "end": v(-40.04, -1.59) * mm});
            skArc(sketch, "E245.MirrorCS", {"start": v(13.6, -37.76) * mm, "mid": v(13.78, -37.92) * mm, "end": v(14.01, -37.92) * mm});
            skArc(sketch, "E246.MirrorCS", {"start": v(-18.25, -31.93) * mm, "mid": v(-18.06, -32.23) * mm, "end": v(-18.16, -32.56) * mm});
            skArc(sketch, "E247.MirrorCS", {"start": v(-31.78, -25.22) * mm, "mid": v(-31.87, -24.94) * mm, "end": v(-31.76, -24.68) * mm});
            skArc(sketch, "E248.MirrorCS", {"start": v(-39.69, -4.37) * mm, "mid": v(-39.95, -4.26) * mm, "end": v(-40.08, -4) * mm});
            skArc(sketch, "E249.MirrorCS", {"start": v(-32.78, -22.59) * mm, "mid": v(-33.07, -22.61) * mm, "end": v(-33.3, -22.45) * mm});
            skArc(sketch, "E250.MirrorCS", {"start": v(30.05, -26.9) * mm, "mid": v(30.34, -26.94) * mm, "end": v(30.58, -26.78) * mm});
            skArc(sketch, "E251.MirrorCS", {"start": v(32.78, -22.59) * mm, "mid": v(33.07, -22.61) * mm, "end": v(33.3, -22.45) * mm});
            skArc(sketch, "E252.MirrorCS", {"start": v(-21.38, -30.54) * mm, "mid": v(-21.12, -30.3) * mm, "end": v(-20.77, -30.34) * mm});
            skArc(sketch, "E253.MirrorCS", {"start": v(12.37, -34.6) * mm, "mid": v(12.16, -34.78) * mm, "end": v(12.18, -35.07) * mm});
            skArc(sketch, "E254.MirrorCS", {"start": v(21.38, -30.54) * mm, "mid": v(21.12, -30.3) * mm, "end": v(20.77, -30.34) * mm});
            skLineSegment(sketch, "E255.MirrorCS", {"start": v(34.44, -20.83) * mm, "end": v(33.3, -22.45) * mm});
            skArc(sketch, "E256.MirrorCS", {"start": v(-6.58, -36.24) * mm, "mid": v(-6.37, -36.42) * mm, "end": v(-6.37, -36.7) * mm});
            skArc(sketch, "E257.MirrorCS", {"start": v(-32.35, -18.25) * mm, "mid": v(-32.02, -18.13) * mm, "end": v(-31.71, -18.3) * mm});
            skArc(sketch, "E258.MirrorCS", {"start": v(-4.97, -36.94) * mm, "mid": v(-4.85, -36.6) * mm, "end": v(-4.52, -36.48) * mm});
            skLineSegment(sketch, "E259.MirrorCS", {"start": v(-4.1, -40.2) * mm, "end": v(-2.37, -40.36) * mm});
            skLineSegment(sketch, "E260.MirrorCS", {"start": v(-10.2, -37.16) * mm, "end": v(-10.07, -35.71) * mm});
            skLineSegment(sketch, "E261.MirrorCS", {"start": v(4.1, -40.2) * mm, "end": v(2.37, -40.36) * mm});
            skArc(sketch, "E262.MirrorCS", {"start": v(4.97, -36.94) * mm, "mid": v(4.85, -36.6) * mm, "end": v(4.52, -36.48) * mm});
            skArc(sketch, "E263.MirrorCS", {"start": v(4.1, -40.2) * mm, "mid": v(4.54, -40) * mm, "end": v(4.74, -39.57) * mm});
            skArc(sketch, "E264.MirrorCS", {"start": v(36.37, -4.04) * mm, "mid": v(36.48, -4.37) * mm, "end": v(36.81, -4.5) * mm});
            skArc(sketch, "E265.MirrorCS", {"start": v(37.29, -0.73) * mm, "mid": v(36.94, -0.78) * mm, "end": v(36.75, -1.08) * mm});
            skArc(sketch, "E266.MirrorCS", {"start": v(-35.25, -9.8) * mm, "mid": v(-35.28, -10.15) * mm, "end": v(-35.57, -10.35) * mm});
            skArc(sketch, "E267.MirrorCS", {"start": v(-36.37, -4.04) * mm, "mid": v(-36.48, -4.37) * mm, "end": v(-36.81, -4.5) * mm});
            skArc(sketch, "E268.MirrorCS", {"start": v(-27.36, -24.94) * mm, "mid": v(-27.28, -25.28) * mm, "end": v(-27.5, -25.56) * mm});
            skLineSegment(sketch, "E269.MirrorCS", {"start": v(10.2, -37.16) * mm, "end": v(10.07, -35.71) * mm});
            skArc(sketch, "E270.MirrorCS", {"start": v(-29.82, -22.55) * mm, "mid": v(-29.49, -22.41) * mm, "end": v(-29.17, -22.58) * mm});
            skLineSegment(sketch, "E271.MirrorCS", {"start": v(-10.34, -38.75) * mm, "end": v(-10.2, -37.16) * mm});
            skArc(sketch, "E272.MirrorCS", {"start": v(29.82, -22.55) * mm, "mid": v(29.49, -22.41) * mm, "end": v(29.17, -22.58) * mm});
            skArc(sketch, "E273.MirrorCS", {"start": v(-37.29, -0.73) * mm, "mid": v(-36.94, -0.78) * mm, "end": v(-36.75, -1.08) * mm});
            skArc(sketch, "E274.MirrorCS", {"start": v(-4.1, -40.2) * mm, "mid": v(-4.54, -40) * mm, "end": v(-4.74, -39.57) * mm});
            skLineSegment(sketch, "E275.MirrorCS", {"start": v(10.34, -38.75) * mm, "end": v(10.2, -37.16) * mm});
            skArc(sketch, "E276.MirrorCS", {"start": v(35.25, -9.8) * mm, "mid": v(35.28, -10.15) * mm, "end": v(35.57, -10.35) * mm});
            skLineSegment(sketch, "E277.MirrorCS", {"start": v(-34.44, -20.83) * mm, "end": v(-33.3, -22.45) * mm});
            skLineSegment(sketch, "E278.MirrorCS", {"start": v(-39.36, -8.22) * mm, "end": v(-36.87, -6.78) * mm});
            skLineSegment(sketch, "E279.MirrorCS", {"start": v(31.78, -25.22) * mm, "end": v(30.58, -26.78) * mm});
            skLineSegment(sketch, "E280.MirrorCS", {"start": v(-31.78, -25.22) * mm, "end": v(-30.58, -26.78) * mm});
            skLineSegment(sketch, "E281.MirrorCS", {"start": v(-31.71, -18.3) * mm, "end": v(-30, -20.75) * mm});
            skLineSegment(sketch, "E282.MirrorCS", {"start": v(4.74, -39.57) * mm, "end": v(4.97, -36.94) * mm});
            skLineSegment(sketch, "E283.MirrorCS", {"start": v(16.25, -36.9) * mm, "end": v(15.83, -33.88) * mm});
            skPoint(sketch, "E284.MirrorP", {"position": v(38.75, -10.92) * mm});
            skPoint(sketch, "E285.MirrorP", {"position": v(-21.17, -30.31) * mm});
            skPoint(sketch, "E286.MirrorP", {"position": v(-15.77, -33.49) * mm});
            skPoint(sketch, "E287.MirrorP", {"position": v(40.38, -1.7) * mm});
            skPoint(sketch, "E288.MirrorP", {"position": v(33.1, -22.73) * mm});
            skLineSegment(sketch, "E289.MirrorCS", {"start": v(36.26, -7) * mm, "end": v(35.25, -9.8) * mm});
            skLineSegment(sketch, "E290.MirrorCS", {"start": v(9.65, -35.42) * mm, "end": v(6.58, -36.24) * mm});
            skLineSegment(sketch, "E291.MirrorCS", {"start": v(40.33, -2.04) * mm, "end": v(40.08, -4) * mm});
            skPoint(sketch, "E292.MirrorP", {"position": v(-36.76, -17.27) * mm});
            skPoint(sketch, "E293.MirrorP", {"position": v(-32, -24.94) * mm});
            skPoint(sketch, "E294.MirrorP", {"position": v(-40.04, -4.35) * mm});
            skLineSegment(sketch, "E295.MirrorCS", {"start": v(-32.78, -22.59) * mm, "end": v(-30.17, -21.37) * mm});
            skPoint(sketch, "E296.MirrorP", {"position": v(30.36, -27.06) * mm});
            skLineSegment(sketch, "E297.MirrorCS", {"start": v(-1.93, -40.05) * mm, "end": v(-1.18, -37.27) * mm});
            skLineSegment(sketch, "E298.MirrorCS", {"start": v(36.42, -17.2) * mm, "end": v(33.6, -16.58) * mm});
            skLineSegment(sketch, "E299.MirrorCS", {"start": v(36.75, -1.08) * mm, "end": v(36.37, -4.04) * mm});
            skLineSegment(sketch, "E300.MirrorCS", {"start": v(16.02, -37.27) * mm, "end": v(14.01, -37.92) * mm});
            skPoint(sketch, "E301.MirrorP", {"position": v(-17.83, -32.2) * mm});
            skPoint(sketch, "E302.MirrorP", {"position": v(-10.04, -35.31) * mm});
            skLineSegment(sketch, "E303.MirrorCS", {"start": v(-36.26, -7) * mm, "end": v(-35.25, -9.8) * mm});
            skPoint(sketch, "E304.MirrorP", {"position": v(29.48, -22.18) * mm});
            skPoint(sketch, "E305.MirrorP", {"position": v(10.04, -35.31) * mm});
            skPoint(sketch, "E306.MirrorP", {"position": v(36.31, -4.53) * mm});
            skLineSegment(sketch, "E307.MirrorCS", {"start": v(40.04, -1.59) * mm, "end": v(37.29, -0.73) * mm});
            skLineSegment(sketch, "E308.MirrorCS", {"start": v(39.69, -4.37) * mm, "end": v(36.81, -4.5) * mm});
            skPoint(sketch, "E309.MirrorP", {"position": v(-37.79, -14.8) * mm});
            skPoint(sketch, "E310.MirrorP", {"position": v(-30.36, -27.06) * mm});
            skPoint(sketch, "E311.MirrorP", {"position": v(-40.38, -1.7) * mm});
            skPoint(sketch, "E312.MirrorP", {"position": v(37.79, -14.8) * mm});
            skPoint(sketch, "E313.MirrorP", {"position": v(22.6, -33.54) * mm});
            skPoint(sketch, "E314.MirrorP", {"position": v(15.77, -33.49) * mm});
            skLineSegment(sketch, "E315.MirrorCS", {"start": v(37.65, -15.12) * mm, "end": v(36.9, -16.95) * mm});
            skPoint(sketch, "E316.MirrorP", {"position": v(-2.02, -40.4) * mm});
            skPoint(sketch, "E317.MirrorP", {"position": v(-10.36, -39.03) * mm});
            skLineSegment(sketch, "E318.MirrorCS", {"start": v(-39.55, -8.73) * mm, "end": v(-38.87, -10.59) * mm});
            skPoint(sketch, "E319.MirrorP", {"position": v(36.81, -0.59) * mm});
            skPoint(sketch, "E320.MirrorP", {"position": v(29.72, -21.16) * mm});
            skPoint(sketch, "E321.MirrorP", {"position": v(1.05, -36.79) * mm});
            skLineSegment(sketch, "E322.MirrorCS", {"start": v(13.6, -37.76) * mm, "end": v(12.18, -35.07) * mm});
            skLineSegment(sketch, "E323.MirrorCS", {"start": v(34.45, -13.26) * mm, "end": v(33.3, -16) * mm});
            skPoint(sketch, "E324.MirrorP", {"position": v(-34.64, -12.8) * mm});
            skPoint(sketch, "E325.MirrorP", {"position": v(-29.48, -22.18) * mm});
            skPoint(sketch, "E326.MirrorP", {"position": v(-36.81, -0.59) * mm});
            skLineSegment(sketch, "E327.MirrorCS", {"start": v(-38.4, -10.86) * mm, "end": v(-35.57, -10.35) * mm});
            skPoint(sketch, "E328.MirrorP", {"position": v(13.74, -38.01) * mm});
            skPoint(sketch, "E329.MirrorP", {"position": v(35.08, -10.27) * mm});
            skPoint(sketch, "E330.MirrorP", {"position": v(21.17, -30.31) * mm});
            skLineSegment(sketch, "E331.MirrorCS", {"start": v(15.4, -33.61) * mm, "end": v(12.37, -34.6) * mm});
            skLineSegment(sketch, "E332.MirrorCS", {"start": v(29.17, -22.58) * mm, "end": v(27.36, -24.94) * mm});
            skPoint(sketch, "E333.MirrorP", {"position": v(-36.31, -4.53) * mm});
            skPoint(sketch, "E334.MirrorP", {"position": v(-33.12, -16.47) * mm});
            skPoint(sketch, "E335.MirrorP", {"position": v(-27.05, -25.33) * mm});
            skPoint(sketch, "E336.MirrorP", {"position": v(-1.05, -36.79) * mm});
            skLineSegment(sketch, "E337.MirrorCS", {"start": v(-40.04, -1.59) * mm, "end": v(-37.29, -0.73) * mm});
            skPoint(sketch, "E338.MirrorP", {"position": v(16.3, -37.18) * mm});
            skPoint(sketch, "E339.MirrorP", {"position": v(34.64, -12.8) * mm});
            skPoint(sketch, "E340.MirrorP", {"position": v(32, -24.94) * mm});
            skLineSegment(sketch, "E341.MirrorCS", {"start": v(7.65, -39.47) * mm, "end": v(6.37, -36.7) * mm});
            skLineSegment(sketch, "E342.MirrorCS", {"start": v(32.78, -22.59) * mm, "end": v(30.17, -21.37) * mm});
            skPoint(sketch, "E343.MirrorP", {"position": v(-7.77, -39.72) * mm});
            skLineSegment(sketch, "E344.MirrorCS", {"start": v(-36.75, -1.08) * mm, "end": v(-36.37, -4.04) * mm});
            skPoint(sketch, "E345.MirrorP", {"position": v(17.83, -32.2) * mm});
            skPoint(sketch, "E346.MirrorP", {"position": v(36.76, -17.27) * mm});
            skLineSegment(sketch, "E347.MirrorCS", {"start": v(38.4, -10.86) * mm, "end": v(35.57, -10.35) * mm});
            skPoint(sketch, "E348.MirrorP", {"position": v(-6.2, -36.34) * mm});
            skLineSegment(sketch, "E349.MirrorCS", {"start": v(-40.33, -2.04) * mm, "end": v(-40.08, -4) * mm});
            skPoint(sketch, "E350.MirrorP", {"position": v(4.7, -40.16) * mm});
            skPoint(sketch, "E351.MirrorP", {"position": v(-20.33, -34.96) * mm});
            skPoint(sketch, "E352.MirrorP", {"position": v(-13.74, -38.01) * mm});
            skPoint(sketch, "E353.MirrorP", {"position": v(27.05, -25.33) * mm});
            skLineSegment(sketch, "E354.MirrorCS", {"start": v(20.77, -30.34) * mm, "end": v(18.25, -31.93) * mm});
            skLineSegment(sketch, "E355.MirrorCS", {"start": v(-34.39, -20.3) * mm, "end": v(-32.35, -18.25) * mm});
            skLineSegment(sketch, "E356.MirrorCS", {"start": v(4.52, -36.48) * mm, "end": v(1.55, -36.74) * mm});
            skLineSegment(sketch, "E357.MirrorCS", {"start": v(39.55, -8.73) * mm, "end": v(38.87, -10.59) * mm});
            skLineSegment(sketch, "E358.MirrorCS", {"start": v(10.09, -39.1) * mm, "end": v(8.05, -39.65) * mm});
            skLineSegment(sketch, "E359.MirrorCS", {"start": v(-31.76, -24.68) * mm, "end": v(-29.82, -22.55) * mm});
            skLineSegment(sketch, "E360.MirrorCS", {"start": v(-4.74, -39.57) * mm, "end": v(-4.97, -36.94) * mm});
            skLineSegment(sketch, "E361.MirrorCS", {"start": v(-37.65, -15.12) * mm, "end": v(-36.9, -16.95) * mm});
            skLineSegment(sketch, "E362.MirrorCS", {"start": v(-37.5, -14.6) * mm, "end": v(-35.06, -13.06) * mm});
            skPoint(sketch, "E363.MirrorP", {"position": v(-29.72, -21.16) * mm});
            skPoint(sketch, "E364.MirrorP", {"position": v(-35.08, -10.27) * mm});
            skPoint(sketch, "E365.MirrorP", {"position": v(7.77, -39.72) * mm});
            skPoint(sketch, "E366.MirrorP", {"position": v(10.36, -39.03) * mm});
            skPoint(sketch, "E367.MirrorP", {"position": v(32, -17.9) * mm});
            skPoint(sketch, "E368.MirrorP", {"position": v(-34.64, -20.54) * mm});
            skPoint(sketch, "E369.MirrorP", {"position": v(-39.67, -8.4) * mm});
            skLineSegment(sketch, "E370.MirrorCS", {"start": v(-13.6, -37.76) * mm, "end": v(-12.18, -35.07) * mm});
            skPoint(sketch, "E371.MirrorP", {"position": v(-22.6, -33.54) * mm});
            skPoint(sketch, "E372.MirrorP", {"position": v(-12, -34.71) * mm});
            skLineSegment(sketch, "E373.MirrorCS", {"start": v(34.39, -20.3) * mm, "end": v(32.35, -18.25) * mm});
            skLineSegment(sketch, "E374.MirrorCS", {"start": v(31.71, -18.3) * mm, "end": v(30, -20.75) * mm});
            skPoint(sketch, "E375.MirrorP", {"position": v(2.02, -40.4) * mm});
            skLineSegment(sketch, "E376.MirrorCS", {"start": v(-20.77, -30.34) * mm, "end": v(-18.25, -31.93) * mm});
            skLineSegment(sketch, "E377.MirrorCS", {"start": v(-22.47, -33.21) * mm, "end": v(-21.38, -30.54) * mm});
            skLineSegment(sketch, "E378.MirrorCS", {"start": v(20.05, -34.65) * mm, "end": v(18.16, -32.56) * mm});
            skPoint(sketch, "E379.MirrorP", {"position": v(34.64, -20.54) * mm});
            skPoint(sketch, "E380.MirrorP", {"position": v(-36.43, -6.53) * mm});
            skLineSegment(sketch, "E381.MirrorCS", {"start": v(-10.09, -39.1) * mm, "end": v(-8.05, -39.65) * mm});
            skLineSegment(sketch, "E382.MirrorCS", {"start": v(-7.65, -39.47) * mm, "end": v(-6.37, -36.7) * mm});
            skLineSegment(sketch, "E383.MirrorCS", {"start": v(-9.65, -35.42) * mm, "end": v(-6.58, -36.24) * mm});
            skLineSegment(sketch, "E384.MirrorCS", {"start": v(22.47, -33.21) * mm, "end": v(21.38, -30.54) * mm});
            skLineSegment(sketch, "E385.MirrorCS", {"start": v(37.5, -14.6) * mm, "end": v(35.06, -13.06) * mm});
            skPoint(sketch, "E386.MirrorP", {"position": v(12, -34.71) * mm});
            skPoint(sketch, "E387.MirrorP", {"position": v(6.2, -36.34) * mm});
            skLineSegment(sketch, "E388.MirrorCS", {"start": v(-16.02, -37.27) * mm, "end": v(-14.01, -37.92) * mm});
            skPoint(sketch, "E389.MirrorP", {"position": v(40.04, -4.35) * mm});
            skLineSegment(sketch, "E390.MirrorCS", {"start": v(-20.05, -34.65) * mm, "end": v(-18.16, -32.56) * mm});
            skLineSegment(sketch, "E391.MirrorCS", {"start": v(-4.52, -36.48) * mm, "end": v(-1.55, -36.74) * mm});
            skLineSegment(sketch, "E392.MirrorCS", {"start": v(-29.17, -22.58) * mm, "end": v(-27.36, -24.94) * mm});
            skLineSegment(sketch, "E393.MirrorCS", {"start": v(-34.45, -13.26) * mm, "end": v(-33.3, -16) * mm});
            skLineSegment(sketch, "E394.MirrorCS", {"start": v(39.36, -8.22) * mm, "end": v(36.87, -6.78) * mm});
            skLineSegment(sketch, "E395.MirrorCS", {"start": v(30.05, -26.9) * mm, "end": v(27.5, -25.56) * mm});
            skPoint(sketch, "E396.MirrorP", {"position": v(33.12, -16.47) * mm});
            skLineSegment(sketch, "E397.MirrorCS", {"start": v(1.93, -40.05) * mm, "end": v(1.18, -37.27) * mm});
            skPoint(sketch, "E398.MirrorP", {"position": v(39.67, -8.4) * mm});
            skLineSegment(sketch, "E399.MirrorCS", {"start": v(-30.05, -26.9) * mm, "end": v(-27.5, -25.56) * mm});
            skLineSegment(sketch, "E400.MirrorCS", {"start": v(-36.42, -17.2) * mm, "end": v(-33.6, -16.58) * mm});
            skLineSegment(sketch, "E401.MirrorCS", {"start": v(-15.4, -33.61) * mm, "end": v(-12.37, -34.6) * mm});
            skLineSegment(sketch, "E402.MirrorCS", {"start": v(-16.25, -36.9) * mm, "end": v(-15.83, -33.88) * mm});
            skLineSegment(sketch, "E403.MirrorCS", {"start": v(31.76, -24.68) * mm, "end": v(29.82, -22.55) * mm});
            skPoint(sketch, "E404.MirrorP", {"position": v(-4.7, -40.16) * mm});
            skPoint(sketch, "E405.MirrorP", {"position": v(20.33, -34.96) * mm});
            skPoint(sketch, "E406.MirrorP", {"position": v(-38.12, -7.5) * mm});
            skLineSegment(sketch, "E407.MirrorCS", {"start": v(-39.69, -4.37) * mm, "end": v(-36.81, -4.5) * mm});
            skPoint(sketch, "E408.MirrorP", {"position": v(-33.1, -22.73) * mm});
            skPoint(sketch, "E409.MirrorP", {"position": v(36.43, -6.53) * mm});
            skPoint(sketch, "E410.MirrorP", {"position": v(-16.3, -37.18) * mm});
            skLineSegment(sketch, "E411.MirrorCS", {"start": v(0, -38.16) * mm, "end": v(0, 0) * mm});
            skPoint(sketch, "E412.MirrorP", {"position": v(-38.75, -10.92) * mm});
            skPoint(sketch, "E413.MirrorP", {"position": v(-32, -17.9) * mm});
            skLineSegment(sketch, "E414", {"start": v(-25.02, 26.6) * mm, "end": v(-22.9, 28.7) * mm});
            skLineSegment(sketch, "E415", {"start": v(-27.3, 29.05) * mm, "end": v(-25.66, 26.67) * mm});
            skLineSegment(sketch, "E416", {"start": v(-27.24, 29.58) * mm, "end": v(-25.88, 30.92) * mm});
            skLineSegment(sketch, "E417", {"start": v(-25.24, 30.97) * mm, "end": v(-22.95, 29.33) * mm});
            skPoint(sketch, "E418.visualSharp", {"position": v(-25.58, 31.21) * mm});
            skArc(sketch, "E418.filletArc", {"start": v(-25.24, 30.97) * mm, "mid": v(-25.57, 31.06) * mm, "end": v(-25.88, 30.92) * mm});
            skPoint(sketch, "E419.visualSharp", {"position": v(-27.5, 29.33) * mm});
            skArc(sketch, "E419.filletArc", {"start": v(-27.24, 29.58) * mm, "mid": v(-27.37, 29.32) * mm, "end": v(-27.3, 29.05) * mm});
            skPoint(sketch, "E420.visualSharp", {"position": v(-25.4, 26.5) * mm});
            skArc(sketch, "E420.filletArc", {"start": v(-25.66, 26.67) * mm, "mid": v(-25.36, 26.49) * mm, "end": v(-25.02, 26.6) * mm});
            skPoint(sketch, "E421.visualSharp", {"position": v(-22.54, 29.04) * mm});
            skArc(sketch, "E421.filletArc", {"start": v(-22.9, 28.7) * mm, "mid": v(-22.78, 29.03) * mm, "end": v(-22.95, 29.33) * mm});
            skLineSegment(sketch, "E422", {"start": v(23.07, 28.6) * mm, "end": v(25.07, 26.4) * mm});
            skLineSegment(sketch, "E423", {"start": v(25.6, 30.77) * mm, "end": v(23.16, 29.24) * mm});
            skLineSegment(sketch, "E424", {"start": v(26.13, 30.7) * mm, "end": v(27.41, 29.29) * mm});
            skLineSegment(sketch, "E425", {"start": v(27.44, 28.64) * mm, "end": v(25.71, 26.42) * mm});
            skPoint(sketch, "E426.visualSharp", {"position": v(27.7, 28.97) * mm});
            skArc(sketch, "E426.filletArc", {"start": v(27.44, 28.64) * mm, "mid": v(27.54, 28.97) * mm, "end": v(27.41, 29.29) * mm});
            skPoint(sketch, "E427.visualSharp", {"position": v(25.9, 30.96) * mm});
            skArc(sketch, "E427.filletArc", {"start": v(26.13, 30.7) * mm, "mid": v(25.88, 30.83) * mm, "end": v(25.6, 30.77) * mm});
            skPoint(sketch, "E428.visualSharp", {"position": v(22.97, 29) * mm});
            skArc(sketch, "E428.filletArc", {"start": v(23.16, 29.24) * mm, "mid": v(22.97, 28.94) * mm, "end": v(23.07, 28.6) * mm});
            skPoint(sketch, "E429.visualSharp", {"position": v(25.4, 26.03) * mm});
            skArc(sketch, "E429.filletArc", {"start": v(25.07, 26.4) * mm, "mid": v(25.4, 26.26) * mm, "end": v(25.71, 26.42) * mm});
            skLineSegment(sketch, "E430", {"start": v(25.59, -26.9) * mm, "end": v(23.38, -28.9) * mm});
            skLineSegment(sketch, "E431", {"start": v(27.76, -29.42) * mm, "end": v(26.22, -26.98) * mm});
            skLineSegment(sketch, "E432", {"start": v(27.68, -29.96) * mm, "end": v(26.27, -31.23) * mm});
            skLineSegment(sketch, "E433", {"start": v(25.62, -31.26) * mm, "end": v(23.4, -29.53) * mm});
            skPoint(sketch, "E434.visualSharp", {"position": v(25.96, -31.52) * mm});
            skArc(sketch, "E434.filletArc", {"start": v(25.62, -31.26) * mm, "mid": v(25.95, -31.36) * mm, "end": v(26.27, -31.23) * mm});
            skPoint(sketch, "E435.visualSharp", {"position": v(27.94, -29.72) * mm});
            skArc(sketch, "E435.filletArc", {"start": v(27.68, -29.96) * mm, "mid": v(27.82, -29.7) * mm, "end": v(27.76, -29.42) * mm});
            skPoint(sketch, "E436.visualSharp", {"position": v(25.98, -26.8) * mm});
            skArc(sketch, "E436.filletArc", {"start": v(26.22, -26.98) * mm, "mid": v(25.93, -26.79) * mm, "end": v(25.59, -26.9) * mm});
            skPoint(sketch, "E437.visualSharp", {"position": v(23.01, -29.23) * mm});
            skArc(sketch, "E437.filletArc", {"start": v(23.38, -28.9) * mm, "mid": v(23.24, -29.22) * mm, "end": v(23.4, -29.53) * mm});
            skLineSegment(sketch, "E438", {"start": v(-22.97, -29) * mm, "end": v(-25.23, -27.06) * mm});
            skLineSegment(sketch, "E439", {"start": v(-25.21, -31.47) * mm, "end": v(-22.98, -29.64) * mm});
            skLineSegment(sketch, "E440", {"start": v(-25.75, -31.46) * mm, "end": v(-27.2, -30.22) * mm});
            skLineSegment(sketch, "E441", {"start": v(-27.3, -29.58) * mm, "end": v(-25.86, -27.16) * mm});
            skPoint(sketch, "E442.visualSharp", {"position": v(-27.52, -29.94) * mm});
            skArc(sketch, "E442.filletArc", {"start": v(-27.3, -29.58) * mm, "mid": v(-27.36, -29.92) * mm, "end": v(-27.2, -30.22) * mm});
            skPoint(sketch, "E443.visualSharp", {"position": v(-25.48, -31.69) * mm});
            skArc(sketch, "E443.filletArc", {"start": v(-25.75, -31.46) * mm, "mid": v(-25.48, -31.56) * mm, "end": v(-25.21, -31.47) * mm});
            skPoint(sketch, "E444.visualSharp", {"position": v(-22.83, -29.37) * mm});
            skArc(sketch, "E444.filletArc", {"start": v(-22.98, -29.64) * mm, "mid": v(-22.83, -29.32) * mm, "end": v(-22.97, -29) * mm});
            skPoint(sketch, "E445.visualSharp", {"position": v(-25.61, -26.73) * mm});
            skArc(sketch, "E445.filletArc", {"start": v(-25.23, -27.06) * mm, "mid": v(-25.57, -26.96) * mm, "end": v(-25.86, -27.16) * mm});
            skSolve(sketch);
        }
        {
            var Q0;
            Q0 = qSketchRegion(id + "F4", true);
            extrude(context, id + "F5", {"entities" : qUnion([Q0]), "operationType" : NewBodyOperationType.ADD, "depth" : 12.7 * mm});
        }
        {
            var Q0;
            Q0=qCreatedBy(makeId("Front.planeOp"),FACE);
            var sketch = newSketch(context, id + "F6", { "sketchPlane" : qUnion([Q0])});
            skLineSegment(sketch, "E446", {"start": v(-62.13, 73.15) * mm, "end": v(-61.86, 71.14) * mm});
            skLineSegment(sketch, "E447", {"start": v(-61.72, 73.8) * mm, "end": v(-60.31, 74.24) * mm});
            skLineSegment(sketch, "E448", {"start": v(-59.6, 73.95) * mm, "end": v(-58.67, 72.15) * mm});
            skLineSegment(sketch, "E449", {"start": v(-59.02, 71.3) * mm, "end": v(-61.1, 70.65) * mm});
            skPoint(sketch, "E450.visualSharp", {"position": v(-62.2, 73.65) * mm});
            skArc(sketch, "E450.filletArc", {"start": v(-61.72, 73.8) * mm, "mid": v(-62.04, 73.55) * mm, "end": v(-62.13, 73.15) * mm});
            skPoint(sketch, "E451.visualSharp", {"position": v(-61.77, 70.44) * mm});
            skArc(sketch, "E451.filletArc", {"start": v(-61.86, 71.14) * mm, "mid": v(-61.6, 70.72) * mm, "end": v(-61.1, 70.65) * mm});
            skPoint(sketch, "E452.visualSharp", {"position": v(-59.84, 74.39) * mm});
            skArc(sketch, "E452.filletArc", {"start": v(-59.6, 73.95) * mm, "mid": v(-59.9, 74.22) * mm, "end": v(-60.31, 74.24) * mm});
            skPoint(sketch, "E453.visualSharp", {"position": v(-58.34, 71.52) * mm});
            skArc(sketch, "E453.filletArc", {"start": v(-59.02, 71.3) * mm, "mid": v(-58.65, 71.65) * mm, "end": v(-58.67, 72.15) * mm});
            skCircle(sketch, "E454", {"center": v(-56.5, 53.44) * mm, "radius": 17.8 * mm});
            skLineSegment(sketch, "E455", {"start": v(-75.79, 53.11) * mm, "end": v(-37.6, 53.11) * mm});
            skLineSegment(sketch, "E456", {"start": v(-68.64, 69.6) * mm, "end": v(-67.78, 67.75) * mm});
            skLineSegment(sketch, "E457", {"start": v(-68.44, 70.33) * mm, "end": v(-67.23, 71.17) * mm});
            skLineSegment(sketch, "E458", {"start": v(-66.47, 71.1) * mm, "end": v(-65.04, 69.67) * mm});
            skLineSegment(sketch, "E459", {"start": v(-65.11, 68.77) * mm, "end": v(-66.9, 67.51) * mm});
            skPoint(sketch, "E460.visualSharp", {"position": v(-68.85, 70.04) * mm});
            skArc(sketch, "E460.filletArc", {"start": v(-68.44, 70.33) * mm, "mid": v(-68.67, 70) * mm, "end": v(-68.64, 69.6) * mm});
            skPoint(sketch, "E461.visualSharp", {"position": v(-67.48, 67.1) * mm});
            skArc(sketch, "E461.filletArc", {"start": v(-67.78, 67.75) * mm, "mid": v(-67.4, 67.43) * mm, "end": v(-66.9, 67.51) * mm});
            skPoint(sketch, "E462.visualSharp", {"position": v(-66.82, 71.46) * mm});
            skArc(sketch, "E462.filletArc", {"start": v(-66.47, 71.1) * mm, "mid": v(-66.84, 71.28) * mm, "end": v(-67.23, 71.17) * mm});
            skPoint(sketch, "E463.visualSharp", {"position": v(-64.54, 69.17) * mm});
            skArc(sketch, "E463.filletArc", {"start": v(-65.11, 68.77) * mm, "mid": v(-64.86, 69.2) * mm, "end": v(-65.04, 69.67) * mm});
            skLineSegment(sketch, "E464", {"start": v(-73.34, 64.95) * mm, "end": v(-72.04, 63.4) * mm});
            skLineSegment(sketch, "E465", {"start": v(-73.34, 65.71) * mm, "end": v(-72.4, 66.84) * mm});
            skLineSegment(sketch, "E466", {"start": v(-71.64, 66.98) * mm, "end": v(-69.88, 65.96) * mm});
            skLineSegment(sketch, "E467", {"start": v(-69.73, 65.07) * mm, "end": v(-71.13, 63.4) * mm});
            skPoint(sketch, "E468.visualSharp", {"position": v(-73.66, 65.33) * mm});
            skArc(sketch, "E468.filletArc", {"start": v(-73.34, 65.71) * mm, "mid": v(-73.48, 65.33) * mm, "end": v(-73.34, 64.95) * mm});
            skPoint(sketch, "E469.visualSharp", {"position": v(-71.58, 62.85) * mm});
            skArc(sketch, "E469.filletArc", {"start": v(-72.04, 63.4) * mm, "mid": v(-71.58, 63.18) * mm, "end": v(-71.13, 63.4) * mm});
            skPoint(sketch, "E470.visualSharp", {"position": v(-72.07, 67.22) * mm});
            skArc(sketch, "E470.filletArc", {"start": v(-71.64, 66.98) * mm, "mid": v(-72.04, 67.05) * mm, "end": v(-72.4, 66.84) * mm});
            skPoint(sketch, "E471.visualSharp", {"position": v(-69.27, 65.6) * mm});
            skArc(sketch, "E471.filletArc", {"start": v(-69.73, 65.07) * mm, "mid": v(-69.6, 65.55) * mm, "end": v(-69.88, 65.96) * mm});
            skLineSegment(sketch, "E472", {"start": v(-75.98, 59.84) * mm, "end": v(-74.32, 58.67) * mm});
            skLineSegment(sketch, "E473", {"start": v(-76.18, 60.57) * mm, "end": v(-75.56, 61.91) * mm});
            skLineSegment(sketch, "E474", {"start": v(-74.87, 62.23) * mm, "end": v(-72.9, 61.7) * mm});
            skLineSegment(sketch, "E475", {"start": v(-72.52, 60.88) * mm, "end": v(-73.44, 58.9) * mm});
            skPoint(sketch, "E476.visualSharp", {"position": v(-82.6, 57.55) * mm});
            skArc(sketch, "E476.filletArc", {"start": v(-76.18, 60.57) * mm, "mid": v(-76.22, 60.17) * mm, "end": v(-75.98, 59.84) * mm});
            skPoint(sketch, "E477.visualSharp", {"position": v(-79.57, 56.45) * mm});
            skArc(sketch, "E477.filletArc", {"start": v(-74.32, 58.67) * mm, "mid": v(-73.83, 58.58) * mm, "end": v(-73.44, 58.9) * mm});
            skPoint(sketch, "E478.visualSharp", {"position": v(-75.35, 62.36) * mm});
            skArc(sketch, "E478.filletArc", {"start": v(-74.87, 62.23) * mm, "mid": v(-75.27, 62.2) * mm, "end": v(-75.56, 61.91) * mm});
            skPoint(sketch, "E479.visualSharp", {"position": v(-72.22, 61.52) * mm});
            skArc(sketch, "E479.filletArc", {"start": v(-72.52, 60.88) * mm, "mid": v(-72.52, 61.38) * mm, "end": v(-72.9, 61.7) * mm});
            skLineSegment(sketch, "E480", {"start": v(-77.17, 54.82) * mm, "end": v(-75.26, 54.12) * mm});
            skLineSegment(sketch, "E481", {"start": v(-77.55, 55.48) * mm, "end": v(-77.29, 56.93) * mm});
            skLineSegment(sketch, "E482", {"start": v(-76.7, 57.42) * mm, "end": v(-74.67, 57.42) * mm});
            skLineSegment(sketch, "E483", {"start": v(-74.1, 56.73) * mm, "end": v(-74.47, 54.58) * mm});
            skPoint(sketch, "E484.visualSharp", {"position": v(-77.63, 54.99) * mm});
            skArc(sketch, "E484.filletArc", {"start": v(-77.55, 55.48) * mm, "mid": v(-77.48, 55.08) * mm, "end": v(-77.17, 54.82) * mm});
            skPoint(sketch, "E485.visualSharp", {"position": v(-74.6, 53.88) * mm});
            skArc(sketch, "E485.filletArc", {"start": v(-75.26, 54.12) * mm, "mid": v(-74.76, 54.17) * mm, "end": v(-74.47, 54.58) * mm});
            skPoint(sketch, "E486.visualSharp", {"position": v(-77.2, 57.42) * mm});
            skArc(sketch, "E486.filletArc", {"start": v(-76.7, 57.42) * mm, "mid": v(-77.09, 57.28) * mm, "end": v(-77.29, 56.93) * mm});
            skPoint(sketch, "E487.visualSharp", {"position": v(-73.97, 57.42) * mm});
            skArc(sketch, "E487.filletArc", {"start": v(-74.1, 56.73) * mm, "mid": v(-74.22, 57.21) * mm, "end": v(-74.67, 57.42) * mm});
            skLineSegment(sketch, "E488.0", {"start": v(-74.6, 53.88) * mm, "end": v(-73.97, 57.42) * mm, "construction": true});
            skLineSegment(sketch, "E489.0", {"start": v(-71.58, 62.85) * mm, "end": v(-69.27, 65.6) * mm, "construction": true});
            skLineSegment(sketch, "E490.0", {"start": v(-67.48, 67.1) * mm, "end": v(-64.54, 69.17) * mm, "construction": true});
            skLineSegment(sketch, "E491.0", {"start": v(-61.77, 70.44) * mm, "end": v(-58.34, 71.52) * mm, "construction": true});
            skLineSegment(sketch, "E492", {"start": v(-56.69, 72.08) * mm, "end": v(-56.5, -7.99) * mm});
            skArc(sketch, "E493.MirrorCS", {"start": v(-39.21, 56.8) * mm, "mid": v(-39.09, 57.3) * mm, "end": v(-38.63, 57.5) * mm});
            skArc(sketch, "E494.MirrorCS", {"start": v(-36.6, 57.51) * mm, "mid": v(-36.22, 57.38) * mm, "end": v(-36.02, 57.03) * mm});
            skArc(sketch, "E495.MirrorCS", {"start": v(-43.62, 65.13) * mm, "mid": v(-43.75, 65.6) * mm, "end": v(-43.46, 66.02) * mm});
            skArc(sketch, "E496.MirrorCS", {"start": v(-38.04, 54.2) * mm, "mid": v(-38.54, 54.25) * mm, "end": v(-38.83, 54.66) * mm});
            skArc(sketch, "E497.MirrorCS", {"start": v(-44.93, 70.38) * mm, "mid": v(-44.7, 70.05) * mm, "end": v(-44.73, 69.65) * mm});
            skLineSegment(sketch, "E498.MirrorCS", {"start": v(-44.73, 69.65) * mm, "end": v(-45.58, 67.8) * mm});
            skLineSegment(sketch, "E499.MirrorCS", {"start": v(-44.93, 70.38) * mm, "end": v(-46.14, 71.22) * mm});
            skLineSegment(sketch, "E500.MirrorCS", {"start": v(-38.7, 53.96) * mm, "end": v(-39.34, 57.5) * mm, "construction": true});
            skLineSegment(sketch, "E501.MirrorCS", {"start": v(-37.34, 59.93) * mm, "end": v(-39, 58.75) * mm});
            skLineSegment(sketch, "E502.MirrorCS", {"start": v(-41.75, 62.92) * mm, "end": v(-44.07, 65.66) * mm, "construction": true});
            skLineSegment(sketch, "E503.MirrorCS", {"start": v(-35.75, 55.57) * mm, "end": v(-36.02, 57.03) * mm});
            skLineSegment(sketch, "E504.MirrorCS", {"start": v(-43.62, 65.13) * mm, "end": v(-42.2, 63.46) * mm});
            skArc(sketch, "E505.MirrorCS", {"start": v(-41.7, 67.04) * mm, "mid": v(-41.31, 67.12) * mm, "end": v(-40.96, 66.92) * mm});
            skLineSegment(sketch, "E506.MirrorCS", {"start": v(-39.21, 56.8) * mm, "end": v(-38.83, 54.66) * mm});
            skLineSegment(sketch, "E507.MirrorCS", {"start": v(-48.25, 68.8) * mm, "end": v(-46.45, 67.56) * mm});
            skLineSegment(sketch, "E508.MirrorCS", {"start": v(-36.13, 54.91) * mm, "end": v(-38.04, 54.2) * mm});
            skLineSegment(sketch, "E509.MirrorCS", {"start": v(-46.9, 71.15) * mm, "end": v(-48.33, 69.7) * mm});
            skArc(sketch, "E510.MirrorCS", {"start": v(-37.14, 60.66) * mm, "mid": v(-37.1, 60.26) * mm, "end": v(-37.34, 59.93) * mm});
            skLineSegment(sketch, "E511.MirrorCS", {"start": v(-41.7, 67.04) * mm, "end": v(-43.46, 66.02) * mm});
            skLineSegment(sketch, "E512.MirrorCS", {"start": v(-54.36, 71.32) * mm, "end": v(-52.27, 70.67) * mm});
            skLineSegment(sketch, "E513.MirrorCS", {"start": v(-36.6, 57.51) * mm, "end": v(-38.63, 57.5) * mm});
            skArc(sketch, "E514.MirrorCS", {"start": v(-41.3, 63.46) * mm, "mid": v(-41.75, 63.25) * mm, "end": v(-42.2, 63.46) * mm});
            skArc(sketch, "E515.MirrorCS", {"start": v(-46.9, 71.15) * mm, "mid": v(-46.53, 71.32) * mm, "end": v(-46.14, 71.22) * mm});
            skArc(sketch, "E516.MirrorCS", {"start": v(-35.75, 55.57) * mm, "mid": v(-35.82, 55.17) * mm, "end": v(-36.13, 54.91) * mm});
            skArc(sketch, "E517.MirrorCS", {"start": v(-45.58, 67.8) * mm, "mid": v(-45.96, 67.48) * mm, "end": v(-46.45, 67.56) * mm});
            skArc(sketch, "E518.MirrorCS", {"start": v(-39, 58.75) * mm, "mid": v(-39.49, 58.66) * mm, "end": v(-39.87, 58.98) * mm});
            skLineSegment(sketch, "E519.MirrorCS", {"start": v(-40, 65.79) * mm, "end": v(-40.96, 66.92) * mm});
            skLineSegment(sketch, "E520.MirrorCS", {"start": v(-38.46, 62.32) * mm, "end": v(-40.42, 61.78) * mm});
            skArc(sketch, "E521.MirrorCS", {"start": v(-51.5, 71.16) * mm, "mid": v(-51.78, 70.74) * mm, "end": v(-52.27, 70.67) * mm});
            skArc(sketch, "E522.MirrorCS", {"start": v(-54.36, 71.32) * mm, "mid": v(-54.73, 71.65) * mm, "end": v(-54.7, 72.16) * mm});
            skLineSegment(sketch, "E523.MirrorCS", {"start": v(-40, 65.03) * mm, "end": v(-41.3, 63.46) * mm});
            skLineSegment(sketch, "E524.MirrorCS", {"start": v(-37.14, 60.66) * mm, "end": v(-37.77, 62) * mm});
            skLineSegment(sketch, "E525.MirrorCS", {"start": v(-51.6, 70.46) * mm, "end": v(-55.03, 71.53) * mm, "construction": true});
            skLineSegment(sketch, "E526.MirrorCS", {"start": v(-45.87, 67.16) * mm, "end": v(-48.83, 69.2) * mm, "construction": true});
            skArc(sketch, "E527.MirrorCS", {"start": v(-53.78, 73.96) * mm, "mid": v(-53.48, 74.24) * mm, "end": v(-53.08, 74.26) * mm});
            skLineSegment(sketch, "E528.MirrorCS", {"start": v(-51.67, 73.82) * mm, "end": v(-53.08, 74.26) * mm});
            skLineSegment(sketch, "E529.MirrorCS", {"start": v(-51.25, 73.18) * mm, "end": v(-51.5, 71.16) * mm});
            skLineSegment(sketch, "E530.MirrorCS", {"start": v(-53.78, 73.96) * mm, "end": v(-54.7, 72.16) * mm});
            skArc(sketch, "E531.MirrorCS", {"start": v(-40.8, 60.96) * mm, "mid": v(-40.8, 61.46) * mm, "end": v(-40.42, 61.78) * mm});
            skLineSegment(sketch, "E532.MirrorCS", {"start": v(-40.8, 60.96) * mm, "end": v(-39.87, 58.98) * mm});
            skArc(sketch, "E533.MirrorCS", {"start": v(-48.25, 68.8) * mm, "mid": v(-48.5, 69.24) * mm, "end": v(-48.33, 69.7) * mm});
            skArc(sketch, "E534.MirrorCS", {"start": v(-38.46, 62.32) * mm, "mid": v(-38.06, 62.28) * mm, "end": v(-37.77, 62) * mm});
            skArc(sketch, "E535.MirrorCS", {"start": v(-40, 65.79) * mm, "mid": v(-39.86, 65.4) * mm, "end": v(-40, 65.03) * mm});
            skArc(sketch, "E536.MirrorCS", {"start": v(-51.67, 73.82) * mm, "mid": v(-51.34, 73.57) * mm, "end": v(-51.25, 73.18) * mm});
            skPoint(sketch, "E537.MirrorP", {"position": v(-45.87, 67.16) * mm});
            skPoint(sketch, "E538.MirrorP", {"position": v(-37.98, 62.45) * mm});
            skPoint(sketch, "E539.MirrorP", {"position": v(-46.55, 71.5) * mm});
            skPoint(sketch, "E540.MirrorP", {"position": v(-39.68, 65.4) * mm});
            skPoint(sketch, "E541.MirrorP", {"position": v(-35.67, 55.09) * mm});
            skPoint(sketch, "E542.MirrorP", {"position": v(-41.75, 62.92) * mm});
            skPoint(sketch, "E543.MirrorP", {"position": v(-36.1, 57.52) * mm});
            skPoint(sketch, "E544.MirrorP", {"position": v(-41.28, 67.3) * mm});
            skPoint(sketch, "E545.MirrorP", {"position": v(-33.74, 56.55) * mm});
            skPoint(sketch, "E546.MirrorP", {"position": v(-53.55, 74.4) * mm});
            skPoint(sketch, "E547.MirrorP", {"position": v(-38.7, 53.96) * mm});
            skPoint(sketch, "E548.MirrorP", {"position": v(-39.34, 57.5) * mm});
            skPoint(sketch, "E549.MirrorP", {"position": v(-44.07, 65.66) * mm});
            skPoint(sketch, "E550.MirrorP", {"position": v(-41.1, 61.6) * mm});
            skPoint(sketch, "E551.MirrorP", {"position": v(-48.83, 69.2) * mm});
            skPoint(sketch, "E552.MirrorP", {"position": v(-51.2, 73.67) * mm});
            skPoint(sketch, "E553.MirrorP", {"position": v(-55.03, 71.53) * mm});
            skPoint(sketch, "E554.MirrorP", {"position": v(-51.6, 70.46) * mm});
            skPoint(sketch, "E555.MirrorP", {"position": v(-44.52, 70.1) * mm});
            skPoint(sketch, "E556.MirrorP", {"position": v(-30.7, 57.67) * mm});
            skArc(sketch, "E557.MirrorCS", {"start": v(-44.93, 35.84) * mm, "mid": v(-44.7, 36.17) * mm, "end": v(-44.73, 36.58) * mm});
            skLineSegment(sketch, "E558.MirrorCS", {"start": v(-44.73, 36.58) * mm, "end": v(-45.58, 38.42) * mm});
            skLineSegment(sketch, "E559.MirrorCS", {"start": v(-44.93, 35.84) * mm, "end": v(-46.14, 35) * mm});
            skArc(sketch, "E560.MirrorCS", {"start": v(-35.75, 50.65) * mm, "mid": v(-35.82, 51.05) * mm, "end": v(-36.13, 51.3) * mm});
            skArc(sketch, "E561.MirrorCS", {"start": v(-77.55, 50.74) * mm, "mid": v(-77.48, 51.14) * mm, "end": v(-77.17, 51.4) * mm});
            skArc(sketch, "E562.MirrorCS", {"start": v(-72.04, 42.83) * mm, "mid": v(-71.58, 43.04) * mm, "end": v(-71.13, 42.83) * mm});
            skArc(sketch, "E563.MirrorCS", {"start": v(-45.58, 38.42) * mm, "mid": v(-45.96, 38.75) * mm, "end": v(-46.45, 38.66) * mm});
            skArc(sketch, "E564.MirrorCS", {"start": v(-75.26, 52.1) * mm, "mid": v(-74.76, 52.05) * mm, "end": v(-74.47, 51.64) * mm});
            skArc(sketch, "E565.MirrorCS", {"start": v(-71.64, 39.25) * mm, "mid": v(-72.04, 39.18) * mm, "end": v(-72.4, 39.38) * mm});
            skArc(sketch, "E566.MirrorCS", {"start": v(-39, 47.47) * mm, "mid": v(-39.49, 47.56) * mm, "end": v(-39.87, 47.24) * mm});
            skArc(sketch, "E567.MirrorCS", {"start": v(-69.73, 41.16) * mm, "mid": v(-69.6, 40.67) * mm, "end": v(-69.88, 40.26) * mm});
            skArc(sketch, "E568.MirrorCS", {"start": v(-40, 40.43) * mm, "mid": v(-39.86, 40.81) * mm, "end": v(-40, 41.2) * mm});
            skLineSegment(sketch, "E569.MirrorCS", {"start": v(-39.21, 49.42) * mm, "end": v(-38.83, 51.56) * mm});
            skArc(sketch, "E570.MirrorCS", {"start": v(-51.11, 35.7) * mm, "mid": v(-51.33, 36.15) * mm, "end": v(-51.8, 36.28) * mm});
            skArc(sketch, "E571.MirrorCS", {"start": v(-65.11, 37.46) * mm, "mid": v(-64.86, 37.02) * mm, "end": v(-65.04, 36.55) * mm});
            skLineSegment(sketch, "E572.MirrorCS", {"start": v(-51.12, 33.66) * mm, "end": v(-51.11, 35.7) * mm});
            skLineSegment(sketch, "E573.MirrorCS", {"start": v(-77.55, 50.74) * mm, "end": v(-77.29, 49.29) * mm});
            skLineSegment(sketch, "E574.MirrorCS", {"start": v(-66.47, 35.12) * mm, "end": v(-65.04, 36.55) * mm});
            skLineSegment(sketch, "E575.MirrorCS", {"start": v(-77.17, 51.4) * mm, "end": v(-75.26, 52.1) * mm});
            skArc(sketch, "E576.MirrorCS", {"start": v(-39.21, 49.42) * mm, "mid": v(-39.09, 48.93) * mm, "end": v(-38.63, 48.72) * mm});
            skLineSegment(sketch, "E577.MirrorCS", {"start": v(-68.44, 35.9) * mm, "end": v(-67.23, 35.05) * mm});
            skArc(sketch, "E578.MirrorCS", {"start": v(-73.34, 40.51) * mm, "mid": v(-73.48, 40.9) * mm, "end": v(-73.34, 41.27) * mm});
            skLineSegment(sketch, "E579.MirrorCS", {"start": v(-40.8, 45.27) * mm, "end": v(-39.87, 47.24) * mm});
            skLineSegment(sketch, "E580.MirrorCS", {"start": v(-38.7, 52.26) * mm, "end": v(-39.34, 48.72) * mm, "construction": true});
            skArc(sketch, "E581.MirrorCS", {"start": v(-48.25, 37.42) * mm, "mid": v(-48.5, 36.99) * mm, "end": v(-48.33, 36.51) * mm});
            skLineSegment(sketch, "E582.MirrorCS", {"start": v(-37.34, 46.3) * mm, "end": v(-39, 47.47) * mm});
            skArc(sketch, "E583.MirrorCS", {"start": v(-38.46, 43.9) * mm, "mid": v(-38.06, 43.94) * mm, "end": v(-37.77, 44.23) * mm});
            skLineSegment(sketch, "E584.MirrorCS", {"start": v(-41.75, 43.3) * mm, "end": v(-44.07, 40.56) * mm, "construction": true});
            skArc(sketch, "E585.MirrorCS", {"start": v(-76.7, 48.8) * mm, "mid": v(-77.09, 48.94) * mm, "end": v(-77.29, 49.29) * mm});
            skLineSegment(sketch, "E586.MirrorCS", {"start": v(-40, 40.43) * mm, "end": v(-40.96, 39.3) * mm});
            skLineSegment(sketch, "E587.MirrorCS", {"start": v(-35.75, 50.65) * mm, "end": v(-36.02, 49.2) * mm});
            skArc(sketch, "E588.MirrorCS", {"start": v(-74.1, 49.5) * mm, "mid": v(-74.22, 49.01) * mm, "end": v(-74.67, 48.8) * mm});
            skLineSegment(sketch, "E589.MirrorCS", {"start": v(-75.98, 46.39) * mm, "end": v(-74.32, 47.55) * mm});
            skArc(sketch, "E590.MirrorCS", {"start": v(-51.6, 33.08) * mm, "mid": v(-51.26, 33.28) * mm, "end": v(-51.12, 33.66) * mm});
            skLineSegment(sketch, "E591.MirrorCS", {"start": v(-38.46, 43.9) * mm, "end": v(-40.42, 44.44) * mm});
            skLineSegment(sketch, "E592.MirrorCS", {"start": v(-43.62, 41.1) * mm, "end": v(-42.2, 42.76) * mm});
            skLineSegment(sketch, "E593.MirrorCS", {"start": v(-74.6, 52.34) * mm, "end": v(-73.97, 48.8) * mm, "construction": true});
            skLineSegment(sketch, "E594.MirrorCS", {"start": v(-74.87, 44) * mm, "end": v(-72.9, 44.52) * mm});
            skArc(sketch, "E595.MirrorCS", {"start": v(-53.96, 35.9) * mm, "mid": v(-54.37, 35.61) * mm, "end": v(-54.41, 35.11) * mm});
            skLineSegment(sketch, "E596.MirrorCS", {"start": v(-76.18, 45.65) * mm, "end": v(-75.56, 44.31) * mm});
            skArc(sketch, "E597.MirrorCS", {"start": v(-41.7, 39.18) * mm, "mid": v(-41.31, 39.1) * mm, "end": v(-40.96, 39.3) * mm});
            skLineSegment(sketch, "E598.MirrorCS", {"start": v(-71.58, 43.37) * mm, "end": v(-69.27, 40.62) * mm, "construction": true});
            skLineSegment(sketch, "E599.MirrorCS", {"start": v(-72.52, 45.34) * mm, "end": v(-73.44, 47.32) * mm});
            skLineSegment(sketch, "E600.MirrorCS", {"start": v(-40, 41.2) * mm, "end": v(-41.3, 42.76) * mm});
            skLineSegment(sketch, "E601.MirrorCS", {"start": v(-48.25, 37.42) * mm, "end": v(-46.45, 38.66) * mm});
            skLineSegment(sketch, "E602.MirrorCS", {"start": v(-68.64, 36.63) * mm, "end": v(-67.78, 38.47) * mm});
            skLineSegment(sketch, "E603.MirrorCS", {"start": v(-71.64, 39.25) * mm, "end": v(-69.88, 40.26) * mm});
            skLineSegment(sketch, "E604.MirrorCS", {"start": v(-41.7, 39.18) * mm, "end": v(-43.46, 40.2) * mm});
            skArc(sketch, "E605.MirrorCS", {"start": v(-41.3, 42.76) * mm, "mid": v(-41.75, 42.97) * mm, "end": v(-42.2, 42.76) * mm});
            skLineSegment(sketch, "E606.MirrorCS", {"start": v(-53.72, 33.2) * mm, "end": v(-54.41, 35.11) * mm});
            skArc(sketch, "E607.MirrorCS", {"start": v(-46.9, 35.07) * mm, "mid": v(-46.53, 34.9) * mm, "end": v(-46.14, 35) * mm});
            skLineSegment(sketch, "E608.MirrorCS", {"start": v(-74.1, 49.5) * mm, "end": v(-74.47, 51.64) * mm});
            skArc(sketch, "E609.MirrorCS", {"start": v(-40.8, 45.27) * mm, "mid": v(-40.8, 44.77) * mm, "end": v(-40.42, 44.44) * mm});
            skLineSegment(sketch, "E610.MirrorCS", {"start": v(-65.11, 37.46) * mm, "end": v(-66.9, 38.7) * mm});
            skArc(sketch, "E611.MirrorCS", {"start": v(-36.6, 48.7) * mm, "mid": v(-36.22, 48.85) * mm, "end": v(-36.02, 49.2) * mm});
            skLineSegment(sketch, "E612.MirrorCS", {"start": v(-45.87, 39.06) * mm, "end": v(-48.83, 37.02) * mm, "construction": true});
            skArc(sketch, "E613.MirrorCS", {"start": v(-37.14, 45.56) * mm, "mid": v(-37.1, 45.96) * mm, "end": v(-37.34, 46.3) * mm});
            skLineSegment(sketch, "E614.MirrorCS", {"start": v(-73.34, 40.51) * mm, "end": v(-72.4, 39.38) * mm});
            skLineSegment(sketch, "E615.MirrorCS", {"start": v(-36.6, 48.7) * mm, "end": v(-38.63, 48.72) * mm});
            skArc(sketch, "E616.MirrorCS", {"start": v(-66.47, 35.12) * mm, "mid": v(-66.84, 34.94) * mm, "end": v(-67.23, 35.05) * mm});
            skArc(sketch, "E617.MirrorCS", {"start": v(-74.87, 44) * mm, "mid": v(-75.27, 44.03) * mm, "end": v(-75.56, 44.31) * mm});
            skLineSegment(sketch, "E618.MirrorCS", {"start": v(-69.73, 41.16) * mm, "end": v(-71.13, 42.83) * mm});
            skArc(sketch, "E619.MirrorCS", {"start": v(-68.44, 35.9) * mm, "mid": v(-68.67, 36.23) * mm, "end": v(-68.64, 36.63) * mm});
            skArc(sketch, "E620.MirrorCS", {"start": v(-72.52, 45.34) * mm, "mid": v(-72.52, 44.84) * mm, "end": v(-72.9, 44.52) * mm});
            skLineSegment(sketch, "E621.MirrorCS", {"start": v(-76.7, 48.8) * mm, "end": v(-74.67, 48.8) * mm});
            skLineSegment(sketch, "E622.MirrorCS", {"start": v(-46.9, 35.07) * mm, "end": v(-48.33, 36.51) * mm});
            skLineSegment(sketch, "E623.MirrorCS", {"start": v(-67.48, 39.11) * mm, "end": v(-64.54, 37.05) * mm, "construction": true});
            skLineSegment(sketch, "E624.MirrorCS", {"start": v(-51.11, 36.4) * mm, "end": v(-54.65, 35.78) * mm, "construction": true});
            skLineSegment(sketch, "E625.MirrorCS", {"start": v(-53.96, 35.9) * mm, "end": v(-51.8, 36.28) * mm});
            skLineSegment(sketch, "E626.MirrorCS", {"start": v(-73.34, 41.27) * mm, "end": v(-72.04, 42.83) * mm});
            skArc(sketch, "E627.MirrorCS", {"start": v(-38.04, 52.01) * mm, "mid": v(-38.54, 51.97) * mm, "end": v(-38.83, 51.56) * mm});
            skArc(sketch, "E628.MirrorCS", {"start": v(-74.32, 47.55) * mm, "mid": v(-73.83, 47.64) * mm, "end": v(-73.44, 47.32) * mm});
            skLineSegment(sketch, "E629.MirrorCS", {"start": v(-36.13, 51.3) * mm, "end": v(-38.04, 52.01) * mm});
            skLineSegment(sketch, "E630.MirrorCS", {"start": v(-37.14, 45.56) * mm, "end": v(-37.77, 44.23) * mm});
            skArc(sketch, "E631.MirrorCS", {"start": v(-76.18, 45.65) * mm, "mid": v(-76.22, 46.05) * mm, "end": v(-75.98, 46.39) * mm});
            skArc(sketch, "E632.MirrorCS", {"start": v(-53.72, 33.2) * mm, "mid": v(-53.46, 32.9) * mm, "end": v(-53.06, 32.82) * mm});
            skArc(sketch, "E633.MirrorCS", {"start": v(-43.62, 41.1) * mm, "mid": v(-43.75, 40.61) * mm, "end": v(-43.46, 40.2) * mm});
            skArc(sketch, "E634.MirrorCS", {"start": v(-67.78, 38.47) * mm, "mid": v(-67.4, 38.8) * mm, "end": v(-66.9, 38.7) * mm});
            skLineSegment(sketch, "E635.MirrorCS", {"start": v(-51.6, 33.08) * mm, "end": v(-53.06, 32.82) * mm});
            skPoint(sketch, "E636.MirrorP", {"position": v(-64.54, 37.05) * mm});
            skPoint(sketch, "E637.MirrorP", {"position": v(-44.52, 36.13) * mm});
            skPoint(sketch, "E638.MirrorP", {"position": v(-46.55, 34.72) * mm});
            skPoint(sketch, "E639.MirrorP", {"position": v(-72.22, 44.7) * mm});
            skPoint(sketch, "E640.MirrorP", {"position": v(-30.7, 48.55) * mm});
            skPoint(sketch, "E641.MirrorP", {"position": v(-39.68, 40.81) * mm});
            skPoint(sketch, "E642.MirrorP", {"position": v(-73.66, 40.9) * mm});
            skPoint(sketch, "E643.MirrorP", {"position": v(-35.67, 51.14) * mm});
            skPoint(sketch, "E644.MirrorP", {"position": v(-77.63, 51.23) * mm});
            skPoint(sketch, "E645.MirrorP", {"position": v(-41.75, 43.3) * mm});
            skPoint(sketch, "E646.MirrorP", {"position": v(-36.1, 48.7) * mm});
            skPoint(sketch, "E647.MirrorP", {"position": v(-74.6, 52.34) * mm});
            skPoint(sketch, "E648.MirrorP", {"position": v(-77.2, 48.8) * mm});
            skPoint(sketch, "E649.MirrorP", {"position": v(-72.07, 39) * mm});
            skPoint(sketch, "E650.MirrorP", {"position": v(-33.74, 49.67) * mm});
            skPoint(sketch, "E651.MirrorP", {"position": v(-71.58, 43.37) * mm});
            skPoint(sketch, "E652.MirrorP", {"position": v(-53.55, 32.74) * mm});
            skPoint(sketch, "E653.MirrorP", {"position": v(-41.28, 38.93) * mm});
            skPoint(sketch, "E654.MirrorP", {"position": v(-73.97, 48.8) * mm});
            skPoint(sketch, "E655.MirrorP", {"position": v(-44.07, 40.56) * mm});
            skPoint(sketch, "E656.MirrorP", {"position": v(-41.1, 44.63) * mm});
            skPoint(sketch, "E657.MirrorP", {"position": v(-79.57, 49.78) * mm});
            skPoint(sketch, "E658.MirrorP", {"position": v(-75.35, 43.86) * mm});
            skPoint(sketch, "E659.MirrorP", {"position": v(-39.34, 48.72) * mm});
            skPoint(sketch, "E660.MirrorP", {"position": v(-51.12, 33.16) * mm});
            skPoint(sketch, "E661.MirrorP", {"position": v(-45.87, 39.06) * mm});
            skPoint(sketch, "E662.MirrorP", {"position": v(-51.11, 36.4) * mm});
            skPoint(sketch, "E663.MirrorP", {"position": v(-37.98, 43.78) * mm});
            skPoint(sketch, "E664.MirrorP", {"position": v(-66.82, 34.76) * mm});
            skPoint(sketch, "E665.MirrorP", {"position": v(-67.48, 39.11) * mm});
            skPoint(sketch, "E666.MirrorP", {"position": v(-82.6, 48.67) * mm});
            skPoint(sketch, "E667.MirrorP", {"position": v(-68.85, 36.18) * mm});
            skPoint(sketch, "E668.MirrorP", {"position": v(-54.65, 35.78) * mm});
            skPoint(sketch, "E669.MirrorP", {"position": v(-48.83, 37.02) * mm});
            skPoint(sketch, "E670.MirrorP", {"position": v(-38.7, 52.26) * mm});
            skPoint(sketch, "E671.MirrorP", {"position": v(-69.27, 40.62) * mm});
            skArc(sketch, "E672.MirrorCS", {"start": v(-58.13, 35.02) * mm, "mid": v(-58.17, 35.52) * mm, "end": v(-58.58, 35.8) * mm});
            skLineSegment(sketch, "E673.MirrorCS", {"start": v(-58.83, 33.11) * mm, "end": v(-58.13, 35.02) * mm});
            skArc(sketch, "E674.MirrorCS", {"start": v(-59.49, 32.73) * mm, "mid": v(-59.09, 32.8) * mm, "end": v(-58.83, 33.11) * mm});
            skArc(sketch, "E675.MirrorCS", {"start": v(-60.73, 36.19) * mm, "mid": v(-61.22, 36.06) * mm, "end": v(-61.43, 35.6) * mm});
            skLineSegment(sketch, "E676.MirrorCS", {"start": v(-61.43, 33.57) * mm, "end": v(-61.43, 35.6) * mm});
            skLineSegment(sketch, "E677.MirrorCS", {"start": v(-57.89, 35.68) * mm, "end": v(-61.43, 36.31) * mm, "construction": true});
            skLineSegment(sketch, "E678.MirrorCS", {"start": v(-60.73, 36.19) * mm, "end": v(-58.58, 35.8) * mm});
            skArc(sketch, "E679.MirrorCS", {"start": v(-61.43, 33.57) * mm, "mid": v(-61.3, 33.2) * mm, "end": v(-60.94, 32.99) * mm});
            skLineSegment(sketch, "E680.MirrorCS", {"start": v(-59.49, 32.73) * mm, "end": v(-60.94, 32.99) * mm});
            skPoint(sketch, "E681.MirrorP", {"position": v(-61.43, 33.08) * mm});
            skPoint(sketch, "E682.MirrorP", {"position": v(-59, 32.64) * mm});
            skPoint(sketch, "E683.MirrorP", {"position": v(-57.89, 35.68) * mm});
            skPoint(sketch, "E684.MirrorP", {"position": v(-61.43, 36.31) * mm});
            skSolve(sketch);
        }
        {
            var Q0;
            {var subQ1=sQuery(id+"F6.wireOp",EDGE,"E456");Q0=makeQuery(id+"F6.imprint","IMPRINT",FACE,{"disambiguationData":[TD([[makeQuery(id+"F6.imprint","IMPRINT",EDGE,{"derivedFrom":subQ1}),1.0]])]});}
            var Q1;
            {var subQ0=sQuery(id+"F6.wireOp",EDGE,"E464");Q1=makeQuery(id+"F6.imprint","IMPRINT",FACE,{"disambiguationData":[TD([[makeQuery(id+"F6.imprint","IMPRINT",EDGE,{"derivedFrom":subQ0}),1.0]])]});}
            var Q2;
            Q2=makeQuery(id+"F6.imprint","IMPRINT",FACE,{"disambiguationData":[TD([[makeQuery(id+"F6.imprint","IMPRINT",EDGE,{"derivedFrom":sQuery(id+"F6.wireOp",EDGE,"E472")}),1.0]])]});
            var Q3;
            Q3=makeQuery(id+"F6.imprint","IMPRINT",FACE,{"disambiguationData":[TD([[makeQuery(id+"F6.imprint","IMPRINT",EDGE,{"derivedFrom":sQuery(id+"F6.wireOp",EDGE,"E480")}),1.0]])]});
            var Q4;
            Q4=makeQuery(id+"F6.imprint","IMPRINT",FACE,{"disambiguationData":[TD([[makeQuery(id+"F6.imprint","IMPRINT",EDGE,{"derivedFrom":sQuery(id+"F6.wireOp",EDGE,"E561.MirrorCS")}),-1.0]])]});
            var Q5;
            Q5=makeQuery(id+"F6.imprint","IMPRINT",FACE,{"disambiguationData":[TD([[makeQuery(id+"F6.imprint","IMPRINT",EDGE,{"derivedFrom":sQuery(id+"F6.wireOp",EDGE,"E589.MirrorCS")}),-1.0]])]});
            var Q6;
            Q6=makeQuery(id+"F6.imprint","IMPRINT",FACE,{"disambiguationData":[TD([[makeQuery(id+"F6.imprint","IMPRINT",EDGE,{"derivedFrom":sQuery(id+"F6.wireOp",EDGE,"E562.MirrorCS")}),-1.0]])]});
            var Q7;
            Q7=makeQuery(id+"F6.imprint","IMPRINT",FACE,{"disambiguationData":[TD([[makeQuery(id+"F6.imprint","IMPRINT",EDGE,{"derivedFrom":sQuery(id+"F6.wireOp",EDGE,"E571.MirrorCS")}),-1.0]])]});
            var Q8;
            {var subQ5=sQuery(id+"F6.wireOp",EDGE,"E572.MirrorCS");Q8=makeQuery(id+"F6.imprint","IMPRINT",FACE,{"disambiguationData":[TD([[makeQuery(id+"F6.imprint","IMPRINT",EDGE,{"derivedFrom":subQ5}),1.0]])]});}
            var Q9;
            Q9=makeQuery(id+"F6.imprint","IMPRINT",FACE,{"disambiguationData":[TD([[makeQuery(id+"F6.imprint","IMPRINT",EDGE,{"derivedFrom":sQuery(id+"F6.wireOp",EDGE,"E557.MirrorCS")}),1.0]])]});
            var Q10;
            Q10=makeQuery(id+"F6.imprint","IMPRINT",FACE,{"disambiguationData":[TD([[makeQuery(id+"F6.imprint","IMPRINT",EDGE,{"derivedFrom":sQuery(id+"F6.wireOp",EDGE,"E568.MirrorCS")}),1.0]])]});
            var Q11;
            {var subQ0=sQuery(id+"F6.wireOp",EDGE,"E582.MirrorCS");Q11=makeQuery(id+"F6.imprint","IMPRINT",FACE,{"disambiguationData":[TD([[makeQuery(id+"F6.imprint","IMPRINT",EDGE,{"derivedFrom":subQ0}),1.0]])]});}
            var Q12;
            Q12=makeQuery(id+"F6.imprint","IMPRINT",FACE,{"disambiguationData":[TD([[makeQuery(id+"F6.imprint","IMPRINT",EDGE,{"derivedFrom":sQuery(id+"F6.wireOp",EDGE,"E560.MirrorCS")}),1.0]])]});
            var Q13;
            Q13=makeQuery(id+"F6.imprint","IMPRINT",FACE,{"disambiguationData":[TD([[makeQuery(id+"F6.imprint","IMPRINT",EDGE,{"derivedFrom":sQuery(id+"F6.wireOp",EDGE,"E494.MirrorCS")}),-1.0]])]});
            var Q14;
            {var subQ1=sQuery(id+"F6.wireOp",EDGE,"E501.MirrorCS");Q14=makeQuery(id+"F6.imprint","IMPRINT",FACE,{"disambiguationData":[TD([[makeQuery(id+"F6.imprint","IMPRINT",EDGE,{"derivedFrom":subQ1}),-1.0]])]});}
            var Q15;
            Q15=makeQuery(id+"F6.imprint","IMPRINT",FACE,{"disambiguationData":[TD([[makeQuery(id+"F6.imprint","IMPRINT",EDGE,{"derivedFrom":sQuery(id+"F6.wireOp",EDGE,"E505.MirrorCS")}),-1.0]])]});
            var Q16;
            Q16=makeQuery(id+"F6.imprint","IMPRINT",FACE,{"disambiguationData":[TD([[makeQuery(id+"F6.imprint","IMPRINT",EDGE,{"derivedFrom":sQuery(id+"F6.wireOp",EDGE,"E497.MirrorCS")}),-1.0]])]});
            var Q17;
            {var subQ0=sQuery(id+"F6.wireOp",EDGE,"E522.MirrorCS");Q17=makeQuery(id+"F6.imprint","IMPRINT",FACE,{"disambiguationData":[TD([[makeQuery(id+"F6.imprint","IMPRINT",EDGE,{"derivedFrom":subQ0}),-1.0]])]});}
            var Q18;
            Q18=makeQuery(id+"F6.imprint","IMPRINT",FACE,{"disambiguationData":[TD([[makeQuery(id+"F6.imprint","IMPRINT",EDGE,{"derivedFrom":sQuery(id+"F6.wireOp",EDGE,"E446")}),1.0]])]});
            var Q19;
            {var subQ0=sQuery(id+"F6.wireOp",EDGE,"E673.MirrorCS");Q19=makeQuery(id+"F6.imprint","IMPRINT",FACE,{"disambiguationData":[TD([[makeQuery(id+"F6.imprint","IMPRINT",EDGE,{"derivedFrom":subQ0}),1.0]])]});}
            extrude(context, id + "F7", {"entities" : qUnion([Q0, Q1, Q2, Q3, Q4, Q5, Q6, Q7, Q8, Q9, Q10, Q11, Q12, Q13, Q14, Q15, Q16, Q17, Q18, Q19]), "operationType" : NewBodyOperationType.ADD, "depth" : 6.35 * mm});
        }
    });
